FREECAD ASSEMBLY — COMPONENT RECIPES ("cad_assembly")

This assembly document has 12 components, labeled P0..P11 below (a component is one placed body or linked part). 11 of them carry a construction recipe — the FreeCAD feature program that regenerates the part from scratch, quoted from this document or its linked companion documents; the rest are supplied as boundary geometry only. No exploded tour is included for this assembly.
COMPONENT P0 — recipe-attached ("cad_top_frame", a linked part whose construction recipe lives in a companion FreeCAD document of the same project; that document's serialized recipe follows).
Construction recipe (the companion document, serialized — sketch geometry with constraints, then the solid features built on it; lengths are millimeters unless a unit is written):

FCSTD DOCUMENT  (FreeCAD 1.0R38641 +468 (Git))
Label: cad_top_frame
License: All rights reserved
LicenseURL: https://en.wikipedia.org/wiki/All_rights_reserved
objects: PartDesign::Line×8, Part::Feature×1, PartDesign::FeatureBase×1, Sketcher::SketchObject×1, PartDesign::Pocket×1, PartDesign::Body×1
note: 17 computed .brp shape members not serialized (recipe doc carries the construction recipe); baked Part::Feature solids carry a one-line shape summary decoded from their .brp

FEATURE [Part::Feature] Part__Feature  label="step"
  shape: bbox 365.1 x 369.8 x 38.23 mm, 1284 faces (baked)
FEATURE [PartDesign::FeatureBase] BaseFeature
  BaseFeature = -> Part__Feature
  Suppressed = false
FEATURE [Sketcher::SketchObject] Sketch
  ArcFitTolerance = 0
  AttachmentSupport = -> [BaseFeature]
  ExternalGeometry = -> [BaseFeature]
  FullyConstrained = true
  MakeInternals = false
  MapMode = 5
  Placement = pos=(0,0,439.5) rot=(0,0,1;0rad)
  sketch-geometry (6):
    g0: LineSegment [constr] StartX=-149.307 StartY=149.307 StartZ=0 EndX=149.307 EndY=149.307 EndZ=0
    g1: LineSegment [constr] StartX=149.307 StartY=149.307 StartZ=0 EndX=149.307 EndY=-149.307 EndZ=0
    g2: LineSegment [constr] StartX=149.307 StartY=-149.307 StartZ=0 EndX=-149.307 EndY=-149.307 EndZ=0
    g3: LineSegment [constr] StartX=-149.307 StartY=-149.307 StartZ=0 EndX=-149.307 EndY=149.307 EndZ=0
    g4: Circle CenterX=152 CenterY=0 CenterZ=0 NormalX=0 NormalY=0 NormalZ=1 AngleXU=0 Radius=1.5
    g5: Circle CenterX=-152 CenterY=0 CenterZ=0 NormalX=0 NormalY=0 NormalZ=1 AngleXU=0 Radius=1.5
  constraints (16):
    c: Coincident(g0,g1)
    c: Coincident(g1,g2)
    c: Coincident(g2,g3)
    c: Coincident(g3,g0)
    c: Horizontal(g0)
    c: Horizontal(g2)
    c: Vertical(g1)
    c: Vertical(g3)
    c: Coincident(g0,g-3)
    c: Coincident(g1,g-5)
    c: PointOnObject(g4,g-1)
    c: PointOnObject(g5,g-1)
    c: Distance(g5,g-7) = 3.5
    c: Equal(g5,g4)
    c: Radius(g4) = 1.5
    c: Distance(g4,g-8) = 3.5
FEATURE [PartDesign::Pocket] Pocket
  BaseFeature = -> BaseFeature
  Direction = (0,0,-1)
  Length = 5
  Length2 = 5
  Profile = -> Sketch
  ReferenceAxis = -> Sketch [N_Axis]
  Suppressed = false
  Type = 0
FEATURE [PartDesign::Line] HoleAxis_1  label="HoleAxis_motor_right_back"
  AttacherType = Attacher::AttachEngineLine
  AttachmentSupport = -> [Pocket]
  Length = 4.79083
  MapMode = 19
  Placement = pos=(152.8,172.15,419.5) rot=(0,-0.707107,0.707107;3.14159rad)
  ResizeMode = 1
FEATURE [PartDesign::Line] HoleAxis_2  label="HoleAxis_motor_left_back"
  AttacherType = Attacher::AttachEngineLine
  AttachmentSupport = -> [Pocket]
  Length = 4.79083
  MapMode = 19
  Placement = pos=(-152.8,172.15,419.5) rot=(1,0,0;1.5708rad)
  ResizeMode = 1
FEATURE [PartDesign::Line] HoleAxis_3  label="HoleAxis_motor_right_right"
  AttacherType = Attacher::AttachEngineLine
  AttachmentSupport = -> [Pocket]
  Length = 4.79083
  MapMode = 19
  Placement = pos=(172.15,152.8,419.5) rot=(-0.57735,-0.57735,0.57735;2.0944rad)
  ResizeMode = 1
FEATURE [PartDesign::Line] HoleAxis_4  label="HoleAxis_motor_left_left"
  AttacherType = Attacher::AttachEngineLine
  AttachmentSupport = -> [Pocket]
  Length = 4.79083
  MapMode = 19
  Placement = pos=(-172.15,152.8,419.5) rot=(0.57735,0.57735,0.57735;2.0944rad)
  ResizeMode = 1
FEATURE [PartDesign::Line] HoleAxis_5  label="HoleAxis_front_idler_right_front"
  AttacherType = Attacher::AttachEngineLine
  AttachmentSupport = -> [Pocket]
  Length = 4.79083
  MapMode = 19
  Placement = pos=(152.8,-172.15,419.5) rot=(0,0.707107,0.707107;3.14159rad)
  ResizeMode = 1
FEATURE [PartDesign::Line] HoleAxis_6  label="HoleAxis_front_idler_left_front"
  AttacherType = Attacher::AttachEngineLine
  AttachmentSupport = -> [Pocket]
  Length = 4.79083
  MapMode = 19
  Placement = pos=(-152.8,-172.15,419.5) rot=(-1,0,0;1.5708rad)
  ResizeMode = 1
FEATURE [PartDesign::Line] HoleAxis_7  label="HoleAxis_support_right"
  AttacherType = Attacher::AttachEngineLine
  AttachmentSupport = -> [Pocket]
  Length = 4.2272
  MapMode = 19
  Placement = pos=(152,0,436.9) rot=(0,0,1;0rad)
  ResizeMode = 1
FEATURE [PartDesign::Line] HoleAxis_8  label="HoleAxis_support_left"
  AttacherType = Attacher::AttachEngineLine
  AttachmentSupport = -> [Pocket]
  Length = 4.2272
  MapMode = 19
  Placement = pos=(-152,0,436.9) rot=(0,0,1;0rad)
  ResizeMode = 1
FEATURE [PartDesign::Body] Body  label="cad_top_frame"
  AllowCompound = false
  BaseFeature = -> Part__Feature
  Group = -> [BaseFeature,Sketch,Pocket,HoleAxis_1,HoleAxis_2,HoleAxis_3,HoleAxis_4,HoleAxis_5,HoleAxis_6,HoleAxis_7,HoleAxis_8]
  Origin = -> Origin
  Placement = pos=(177.5,177.5,-414.5) rot=(0,0,1;0rad)
  Tip = -> Pocket
COMPONENT P1 — geometry summary ("front_idler_left_part"; no construction recipe available for this part):
  bounding box: 54.7 x 33.8 x 26.2 mm
  tessellated surface: 4,628 triangles
  volume: 28726 mm^3 (59% of its bounding box)
COMPONENT P2 — recipe-attached ("k1_front_idler_right_part", a linked part whose construction recipe lives in a companion FreeCAD document of the same project; that document's serialized recipe follows).
Construction recipe (the companion document, serialized — sketch geometry with constraints, then the solid features built on it; lengths are millimeters unless a unit is written):

FCSTD DOCUMENT  (FreeCAD 1.0R38641 +468 (Git))
Label: k1_front_idler_right
License: All rights reserved
LicenseURL: https://en.wikipedia.org/wiki/All_rights_reserved
objects: PartDesign::Pad×11, PartDesign::Pocket×9, Sketcher::SketchObject×8, PartDesign::Line×2, App::Link×2, Part::Feature×1, PartDesign::FeatureBase×1, PartDesign::Body×1, App::Part×1
note: 82 computed .brp shape members not serialized (recipe doc carries the construction recipe); baked Part::Feature solids carry a one-line shape summary decoded from their .brp
EXTERNAL_REF file=cad_powge_pulley.FCStd obj=Part
EXTERNAL_REF file=cad_M4_DIN912_30mm.FCStd obj=Body

FEATURE [Part::Feature] Part__Feature  label="step"
  shape: bbox 25.99 x 33.8 x 47.95 mm, 40 faces (baked)
FEATURE [PartDesign::FeatureBase] BaseFeature
  BaseFeature = -> Part__Feature
  Suppressed = false
FEATURE [PartDesign::Line] HoleAxis_1  label="HoleAxis_frame"
  AttacherType = Attacher::AttachEngineLine
  AttachmentSupport = -> [BaseFeature]
  Length = 6.48171
  MapMode = 19
  Placement = pos=(-19.485,0,40.055) rot=(1,0,0;1.5708rad)
  ResizeMode = 1
FEATURE [Sketcher::SketchObject] Sketch
  ArcFitTolerance = 1e-06
  AttachmentSupport = -> [BaseFeature]
  ExternalGeometry = -> [BaseFeature]
  FullyConstrained = true
  MakeInternals = false
  MapMode = 5
  Placement = pos=(0,0,36) rot=(1,0,0;3.14159rad)
  sketch-geometry (1):
    g0: Circle CenterX=-11.5 CenterY=-17.6 CenterZ=0 NormalX=0 NormalY=0 NormalZ=1 AngleXU=0 Radius=0.75
  constraints (2):
    c: Coincident(g0,g-3)
    c: Diameter(g0) = 1.5
FEATURE [PartDesign::Pocket] Pocket
  BaseFeature = -> BaseFeature
  Direction = (0,0,1)
  Length = 5
  Length2 = 5
  Profile = -> Sketch
  ReferenceAxis = -> Sketch [N_Axis]
  Refine = true
  Suppressed = false
  Type = 1
FEATURE [PartDesign::Pocket] Pocket001
  BaseFeature = -> Pocket
  Direction = (0,0,-1)
  Length = 0.725
  Length2 = 5
  Profile = -> Pocket [Face18]
  Refine = true
  Suppressed = false
  Type = 0
FEATURE [PartDesign::Pad] Pad
  BaseFeature = -> Pocket001
  Direction = (0,0,-1)
  Length = 0.725
  Length2 = 10
  Profile = -> Pocket001 [Face34]
  Refine = true
  Suppressed = false
  Type = 0
FEATURE [PartDesign::Pad] Pad001
  BaseFeature = -> Pad
  Direction = (0,0,-1)
  Length = 0.725
  Length2 = 10
  Profile = -> Pad [Face20]
  Refine = true
  Suppressed = false
  Type = 0
FEATURE [PartDesign::Pocket] Pocket002
  BaseFeature = -> Pad001
  Direction = (0,0,-1)
  Length = 0.725
  Length2 = 5
  Profile = -> Pad001 [Face29]
  Refine = true
  Suppressed = false
  Type = 0
FEATURE [PartDesign::Pad] Pad002
  BaseFeature = -> Pocket002
  Direction = (-1,0,0)
  Length = 0.21
  Length2 = 10
  Profile = -> Pocket002 [Face4]
  Refine = true
  Suppressed = false
  Type = 0
FEATURE [PartDesign::Line] DatumLine
  AttacherType = Attacher::AttachEngineLine
  AttachmentOffset = pos=(0,0.6,0) rot=(0,0,1;0rad)
  AttachmentSupport = -> [Pad002]
  Length = 20
  MapMode = 19
  Placement = pos=(-20.105,22.365,40.945) rot=(0,0,1;0rad)
  ResizeMode = 0
FEATURE [PartDesign::Pad] Pad003
  BaseFeature = -> Pad002
  Direction = (0,0,-1)
  Length = 10
  Length2 = 10
  Profile = -> Pad002 [Face37]
  Refine = true
  Suppressed = false
  Type = 3
  UpToFace = -> Pad002 [Face35]
FEATURE [PartDesign::Pad] Pad004
  BaseFeature = -> Pad003
  Direction = (0,0,1)
  Length = 10
  Length2 = 10
  Profile = -> Pad003 [Edge84]
  Refine = true
  Suppressed = false
  Type = 3
  UpToFace = -> Pad003 [Face17]
FEATURE [PartDesign::Pad] Pad005
  BaseFeature = -> Pad004
  Direction = (0,0,1)
  Length = 10
  Length2 = 10
  Profile = -> Pad004 [Face20]
  Refine = true
  Suppressed = false
  Type = 3
  UpToFace = -> Pad004 [Face37]
FEATURE [Sketcher::SketchObject] Sketch001
  ArcFitTolerance = 1e-06
  AttachmentSupport = -> [Pad005]
  ExternalGeometry = -> [DatumLine]
  FullyConstrained = true
  MakeInternals = false
  MapMode = 5
  Placement = pos=(0,0,40.945) rot=(0,0,1;0rad)
  sketch-geometry (1):
    g0: Circle CenterX=-20.105 CenterY=22.365 CenterZ=0 NormalX=0 NormalY=0 NormalZ=1 AngleXU=0 Radius=1.6
  constraints (2):
    c: Coincident(g0,g-3)
    c: Diameter(g0) = 3.2
FEATURE [PartDesign::Pocket] Pocket003
  BaseFeature = -> Pad005
  Direction = (0,0,-1)
  Length = 0
  Length2 = 5
  Profile = -> Sketch001
  ReferenceAxis = -> Sketch001 [N_Axis]
  Refine = true
  Suppressed = false
  Type = 3
  UpToFace = -> Pad005 [Face18]
FEATURE [Sketcher::SketchObject] Sketch002
  ArcFitTolerance = 1e-06
  AttachmentSupport = -> [Pocket003]
  ExternalGeometry = -> [DatumLine]
  FullyConstrained = true
  MakeInternals = false
  MapMode = 5
  Placement = pos=(0,0,32.325) rot=(1,0,0;3.14159rad)
  sketch-geometry (1):
    g0: Circle CenterX=-20.105 CenterY=-22.365 CenterZ=0 NormalX=0 NormalY=0 NormalZ=1 AngleXU=0 Radius=2.3
  constraints (2):
    c: Coincident(g0,g-3)
    c: Diameter(g0) = 4.6
FEATURE [PartDesign::Pocket] Pocket004
  BaseFeature = -> Pocket003
  Direction = (0,0,1)
  Length = 5.1
  Length2 = 5
  Profile = -> Sketch002
  ReferenceAxis = -> Sketch002 [N_Axis]
  Refine = true
  Suppressed = false
  Type = 0
FEATURE [Sketcher::SketchObject] Sketch003
  ArcFitTolerance = 1e-06
  AttachmentSupport = -> [Pocket004]
  ExternalGeometry = -> [DatumLine,Pocket004]
  FullyConstrained = true
  MakeInternals = false
  MapMode = 5
  Placement = pos=(0,0,32.325) rot=(1,0,0;3.14159rad)
  sketch-geometry (4):
    g0: ArcOfCircle CenterX=-20.105 CenterY=-22.365 CenterZ=0 NormalX=0 NormalY=0 NormalZ=1 AngleXU=0 Radius=4 StartAngle=0 EndAngle=3.14159
    g1: LineSegment StartX=-16.105 StartY=-22.365 StartZ=0 EndX=-16.105 EndY=-24 EndZ=0
    g2: LineSegment StartX=-16.105 StartY=-24 StartZ=0 EndX=-24.105 EndY=-24 EndZ=0
    g3: LineSegment StartX=-24.105 StartY=-24 StartZ=0 EndX=-24.105 EndY=-22.365 EndZ=0
  constraints (10):
    c: Coincident(g0,g-3)
    c: PointOnObject(g1,g-4)
    c: Vertical(g1)
    c: Coincident(g2,g1)
    c: Horizontal(g2)
    c: Coincident(g3,g2)
    c: Vertical(g3)
    c: Radius(g0) = 4
    c: Tangent(g1,g0) = 1.5708
    c: Tangent(g3,g0) = 1.5708
FEATURE [PartDesign::Pocket] Pocket005
  BaseFeature = -> Pocket004
  Direction = (0,0,1)
  Length = 8
  Length2 = 5
  Profile = -> Sketch003
  ReferenceAxis = -> Sketch003 [N_Axis]
  Refine = true
  Reversed = true
  Suppressed = false
  Type = 0
FEATURE [PartDesign::Pad] Pad006
  BaseFeature = -> Pocket005
  Direction = (0,0,-1)
  Length = 6.72
  Length2 = 10
  Profile = -> Pocket005 [Face12]
  Refine = true
  Suppressed = false
  Type = 0
FEATURE [Sketcher::SketchObject] Sketch004
  ArcFitTolerance = 1e-06
  AttachmentSupport = -> [Pad006]
  ExternalGeometry = -> [Pad006]
  FullyConstrained = true
  MakeInternals = false
  MapMode = 5
  Placement = pos=(0,0,0.2) rot=(1,0,0;3.14159rad)
  sketch-geometry (2):
    g0: Circle CenterX=-11.5 CenterY=-17.6 CenterZ=0 NormalX=0 NormalY=0 NormalZ=1 AngleXU=0 Radius=4.5
    g1: Circle CenterX=-11.5 CenterY=-17.6 CenterZ=0 NormalX=0 NormalY=0 NormalZ=1 AngleXU=0 Radius=1.9
  constraints (4):
    c: Coincident(g0,g-3)
    c: Equal(g0,g-3)
    c: Coincident(g1,g0)
    c: Diameter(g1) = 3.8
FEATURE [PartDesign::Pad] Pad007
  BaseFeature = -> Pad006
  Direction = (0,0,-1)
  Length = 5
  Length2 = 10
  Profile = -> Sketch004
  ReferenceAxis = -> Sketch004 [N_Axis]
  Refine = true
  Reversed = true
  Suppressed = false
  Type = 0
FEATURE [Sketcher::SketchObject] Sketch005
  ArcFitTolerance = 1e-06
  AttachmentSupport = -> [Pad007]
  ExternalGeometry = -> [Pad007]
  FullyConstrained = true
  MakeInternals = false
  MapMode = 5
  Placement = pos=(0,0,0.2) rot=(1,0,0;3.14159rad)
  sketch-geometry (2):
    g0: Circle CenterX=-11.5 CenterY=-17.6 CenterZ=0 NormalX=0 NormalY=0 NormalZ=1 AngleXU=0 Radius=4.5
    g1: Circle CenterX=-11.5 CenterY=-17.6 CenterZ=0 NormalX=0 NormalY=0 NormalZ=1 AngleXU=0 Radius=3.6
  constraints (4):
    c: Coincident(g0,g-3)
    c: Equal(g0,g-3)
    c: Coincident(g1,g0)
    c: Diameter(g1) = 7.2
FEATURE [PartDesign::Pad] Pad008
  BaseFeature = -> Pad007
  Direction = (0,0,-1)
  Length = 10
  Length2 = 10
  Profile = -> Sketch005
  ReferenceAxis = -> Sketch005 [N_Axis]
  Refine = true
  Suppressed = false
  Type = 3
  UpToFace = -> Pad007 [Face1]
FEATURE [PartDesign::Pocket] Pocket006
  BaseFeature = -> Pad008
  Direction = (0,0,-1)
  Length = 0.3
  Length2 = 5
  Profile = -> Pad008 [Face14]
  Refine = true
  Suppressed = false
  Type = 0
FEATURE [PartDesign::Pad] Pad009
  BaseFeature = -> Pocket006
  Direction = (0,0,-1)
  Length = 0.3
  Length2 = 10
  Profile = -> Pocket006 [Face11]
  Refine = true
  Suppressed = false
  Type = 0
FEATURE [PartDesign::Pad] Pad010
  BaseFeature = -> Pad009
  Direction = (0,0,-1)
  Length = 0.3
  Length2 = 10
  Profile = -> Pad009 [Face32]
  Refine = true
  Suppressed = false
  Type = 0
FEATURE [App::Link] Link  label="cad_powge_pulley_link"
  LinkPlacement = pos=(-11.5,17.6,9.7) rot=(0,0,1;0rad)
  LinkedObject = -> <external cad_powge_pulley.FCStd>#Part
  Placement = pos=(-11.5,17.6,9.7) rot=(0,0,1;0rad)
FEATURE [Sketcher::SketchObject] Sketch006
  ArcFitTolerance = 1e-06
  AttachmentSupport = -> [Pad010]
  ExternalGeometry = -> [Pad010]
  FullyConstrained = true
  MakeInternals = false
  MapMode = 5
  Placement = pos=(0,0,47.945) rot=(0,0,1;0rad)
  sketch-geometry (3):
    g0: LineSegment StartX=-26.2 StartY=0 StartZ=0 EndX=-25.2 EndY=0 EndZ=0
    g1: LineSegment StartX=-26.2 StartY=0 StartZ=0 EndX=-26.2 EndY=14.265 EndZ=0
    g2: LineSegment StartX=-26.2 StartY=14.265 StartZ=0 EndX=-25.2 EndY=0 EndZ=0
  constraints (7):
    c: Coincident(g0,g-3)
    c: PointOnObject(g0,g-1)
    c: Coincident(g1,g0)
    c: Coincident(g1,g-3)
    c: Coincident(g2,g1)
    c: Coincident(g2,g0)
    c: Distance(g0,g0) = 1
FEATURE [PartDesign::Pocket] Pocket007
  BaseFeature = -> Pad010
  Direction = (0,0,-1)
  Length = 5
  Length2 = 5
  Profile = -> Sketch006
  ReferenceAxis = -> Sketch006 [N_Axis]
  Refine = true
  Suppressed = false
  Type = 1
FEATURE [App::Link] Link001  label="cad_m4_din912_30_link"
  LinkPlacement = pos=(-11.5,17.6,-3.8) rot=(0,0,1;0rad)
  LinkedObject = -> <external cad_M4_DIN912_30mm.FCStd>#Body
  Placement = pos=(-11.5,17.6,-3.8) rot=(0,0,1;0rad)
FEATURE [Sketcher::SketchObject] Sketch007
  ArcFitTolerance = 1e-06
  AttachmentSupport = -> [Pocket007]
  ExternalGeometry = -> [Pocket007]
  FullyConstrained = true
  MakeInternals = false
  MapMode = 5
  Placement = pos=(0,0,0) rot=(0.57735,0.57735,0.57735;2.0944rad)
  sketch-geometry (2):
    g0: LineSegment [constr] StartX=19.265 StartY=40.055 StartZ=0 EndX=19.265 EndY=4.985 EndZ=0
    g1: Circle CenterX=19.265 CenterY=24.78 CenterZ=0 NormalX=0 NormalY=0 NormalZ=1 AngleXU=0 Radius=2.3
  constraints (5):
    c: Coincident(g0,g-3)
    c: Coincident(g0,g-4)
    c: PointOnObject(g1,g0)
    c: Equal(g1,g-3)
    c: Distance(g1,g-5) = 31.5
FEATURE [PartDesign::Pocket] Pocket008
  BaseFeature = -> Pocket007
  Direction = (-1,0,0)
  Length = 1
  Length2 = 5
  Profile = -> Sketch007
  ReferenceAxis = -> Sketch007 [N_Axis]
  Refine = true
  Suppressed = false
  Type = 0
FEATURE [PartDesign::Body] Body  label="k1_front_idler_right"
  AllowCompound = false
  BaseFeature = -> Part__Feature
  Group = -> [BaseFeature,HoleAxis_1,Sketch,Pocket,Pocket001,Pad,Pad001,Pocket002,Pad002,DatumLine,Pad003,Pad004,Pad005,Sketch001,Pocket003,Sketch002,Pocket004,Sketch003,Pocket005,Pad006,Sketch004,Pad007,Sketch005,Pad008,Pocket006,Pad009,Pad010,Sketch006,Pocket007,Sketch007,Pocket008]
  Origin = -> Origin
  Tip = -> Pocket008
FEATURE [App::Part] Part  label="k1_front_idler_right_part"
  Group = -> [Part__Feature,Body,Link,Link001]
  Origin = -> Origin001
  Placement = pos=(0,0,0) rot=(0,0,1;3.14159rad)
COMPONENT P3 — recipe-attached ("k1_motor_mount_stock_left_part", a linked part whose construction recipe lives in a companion FreeCAD document of the same project; that document's serialized recipe follows).
Construction recipe (the companion document, serialized — sketch geometry with constraints, then the solid features built on it; lengths are millimeters unless a unit is written):

FCSTD DOCUMENT  (FreeCAD 1.0R38641 +468 (Git))
Label: k1_motor_mount_stock_left
License: All rights reserved
LicenseURL: https://en.wikipedia.org/wiki/All_rights_reserved
objects: App::Link×9, PartDesign::Pocket×6, Sketcher::SketchObject×5, PartDesign::Pad×2, Part::Feature×1, PartDesign::FeatureBase×1, PartDesign::Body×1, App::Part×1
note: 38 computed .brp shape members not serialized (recipe doc carries the construction recipe); baked Part::Feature solids carry a one-line shape summary decoded from their .brp
EXTERNAL_REF file=cad_powge_pulley.FCStd obj=Part
EXTERNAL_REF file=cad_mf95zz.FCStd obj=Body
EXTERNAL_REF file=cad_motor_shaft_55mm.FCStd obj=Part__Feature
EXTERNAL_REF file=cad_20T_15mm_pulley.FCStd obj=Part
EXTERNAL_REF file=cad_nema17_42_60.FCStd obj=COMPOUND049
EXTERNAL_REF file=cad_diaphragm_coupler.FCStd obj=_764K239_NO_THREADS_Servomotor_Precision_Flexible_Shaft_Coupling013
EXTERNAL_REF file=cad_m4_35mm.FCStd obj=Part__Feature

FEATURE [Part::Feature] Part__Feature  label="step"
  shape: bbox 73.5 x 47.7 x 110.9 mm, 153 faces (baked)
FEATURE [PartDesign::FeatureBase] BaseFeature
  BaseFeature = -> Part__Feature
  Suppressed = false
FEATURE [App::Link] Link  label="cad_powge_pulley_top_link"
  LinkPlacement = pos=(14.1406,100.078,20.85) rot=(0,0,1;0rad)
  LinkedObject = -> <external cad_powge_pulley.FCStd>#Part
  Placement = pos=(14.1406,100.078,20.85) rot=(0,0,1;0rad)
FEATURE [App::Link] Link001  label="cad_powge_pulley_bottom_link"
  LinkPlacement = pos=(14.1406,100.078,9.7) rot=(0,0,1;0rad)
  LinkedObject = -> <external cad_powge_pulley.FCStd>#Part
  Placement = pos=(14.1406,100.078,9.7) rot=(0,0,1;0rad)
FEATURE [App::Link] Link002  label="cad_mf95zz_top_link"
  LinkPlacement = pos=(29.6406,84.5783,37.2) rot=(0,1,0;3.14159rad)
  LinkedObject = -> <external cad_mf95zz.FCStd>#Body
  Placement = pos=(29.6406,84.5783,37.2) rot=(0,1,0;3.14159rad)
FEATURE [App::Link] Link003  label="cad_mf95zz_bottom_link"
  LinkPlacement = pos=(29.6406,84.5783,-4.4) rot=(0,0,1;3.14159rad)
  LinkedObject = -> <external cad_mf95zz.FCStd>#Body
  Placement = pos=(29.6406,84.5783,-4.4) rot=(0,0,1;3.14159rad)
FEATURE [App::Link] Link004  label="cad_motor_shaft_55mm_link"
  LinkPlacement = pos=(370.445,-290.422,175.11) rot=(0,0,1;0rad)
  LinkedObject = -> <external cad_motor_shaft_55mm.FCStd>#Part__Feature
  Placement = pos=(370.445,-290.422,175.11) rot=(0,0,1;0rad)
FEATURE [App::Link] Link005  label="cad_20T_15mm_pulley_link"
  LinkPlacement = pos=(117.263,15.5011,1.55198) rot=(0,1,0;3.14159rad)
  LinkedObject = -> <external cad_20T_15mm_pulley.FCStd>#Part
  Placement = pos=(117.263,15.5011,1.55198) rot=(0,1,0;3.14159rad)
FEATURE [App::Link] Link006  label="cad_nema17_42_60_link"
  LinkPlacement = pos=(29.6406,84.5783,-79.702) rot=(0,0,1;0rad)
  LinkedObject = -> <external cad_nema17_42_60.FCStd>#COMPOUND049
  Placement = pos=(29.6406,84.5783,-79.702) rot=(0,0,1;0rad)
FEATURE [App::Link] Link007  label="cad_diaphragm_coupler_5_5_link"
  LinkPlacement = pos=(370.37,-290.416,168.405) rot=(0,0,1;0rad)
  LinkedObject = -> <external cad_diaphragm_coupler.FCStd>#_764K239_NO_THREADS_Servomotor_Precision_Flexible_Shaft_Coupling013
  Placement = pos=(370.37,-290.416,168.405) rot=(0,0,1;0rad)
FEATURE [App::Link] Link008  label="cad_m4_35mm_link"
  LinkPlacement = pos=(14.1406,100.078,0.376278) rot=(0,0,1;0rad)
  LinkedObject = -> <external cad_m4_35mm.FCStd>#Part__Feature
  Placement = pos=(14.1406,100.078,0.376278) rot=(0,0,1;0rad)
FEATURE [Sketcher::SketchObject] Sketch
  ArcFitTolerance = 1e-06
  AttachmentSupport = -> [BaseFeature]
  ExternalGeometry = -> [BaseFeature]
  FullyConstrained = true
  MakeInternals = false
  MapMode = 5
  Placement = pos=(8.1168e-12,-2.90335e-11,-57) rot=(0,0,1;0rad)
  sketch-geometry (6):
    g0: LineSegment StartX=52.6406 StartY=970.078 StartZ=0 EndX=59.1406 EndY=963.578 EndZ=0
    g1: LineSegment StartX=100.141 StartY=963.578 StartZ=0 EndX=106.641 EndY=970.078 EndZ=0
    g2: LineSegment StartX=106.641 StartY=970.078 StartZ=0 EndX=106.641 EndY=963.578 EndZ=0
    g3: LineSegment StartX=100.141 StartY=963.578 StartZ=0 EndX=106.641 EndY=963.578 EndZ=0
    g4: LineSegment StartX=52.6406 StartY=970.078 StartZ=0 EndX=52.6406 EndY=963.578 EndZ=0
    g5: LineSegment StartX=59.1406 StartY=963.578 StartZ=0 EndX=52.6406 EndY=963.578 EndZ=0
  constraints (14):
    c: Coincident(g0,g-3)
    c: Coincident(g0,g-4)
    c: Coincident(g1,g-4)
    c: Coincident(g1,g-5)
    c: Coincident(g2,g1)
    c: Vertical(g2)
    c: Coincident(g3,g1)
    c: Coincident(g3,g2)
    c: Horizontal(g3)
    c: Coincident(g4,g0)
    c: Vertical(g4)
    c: Coincident(g5,g0)
    c: Coincident(g5,g4)
    c: Horizontal(g5)
FEATURE [PartDesign::Pocket] Pocket
  BaseFeature = -> BaseFeature
  Direction = (1.424e-13,-5.094e-13,-1)
  Length = 6
  Length2 = 5
  Profile = -> Sketch
  ReferenceAxis = -> Sketch [N_Axis]
  Refine = true
  Suppressed = false
  Type = 0
FEATURE [Sketcher::SketchObject] Sketch001
  ArcFitTolerance = 1e-06
  AttachmentSupport = -> [Pocket]
  ExternalGeometry = -> [Pocket]
  FullyConstrained = true
  MakeInternals = false
  MapMode = 5
  Placement = pos=(4.7e-13,-2.35e-13,-63) rot=(1,0,0;3.14159rad)
  sketch-geometry (2):
    g0: Circle CenterX=79.6406 CenterY=-984.578 CenterZ=0 NormalX=0 NormalY=0 NormalZ=1 AngleXU=0 Radius=15
    g1: Circle CenterX=79.6406 CenterY=-984.578 CenterZ=0 NormalX=0 NormalY=0 NormalZ=1 AngleXU=0 Radius=14
  constraints (4):
    c: Coincident(g0,g-3)
    c: Equal(g0,g-3)
    c: Coincident(g1,g0)
    c: Diameter(g1) = 28
FEATURE [PartDesign::Pad] Pad
  BaseFeature = -> Pocket
  Direction = (7.5e-15,-3.7e-15,-1)
  Length = 10
  Length2 = 10
  Profile = -> Sketch001
  ReferenceAxis = -> Sketch001 [N_Axis]
  Refine = true
  Suppressed = false
  Type = 3
  UpToFace = -> Pocket [Face9]
FEATURE [PartDesign::Pocket] Pocket001
  BaseFeature = -> Pad
  Direction = (7e-15,-2.3e-15,-1)
  Length = 0
  Length2 = 5
  Profile = -> Pad [Face8]
  Refine = true
  Suppressed = false
  Type = 3
  UpToFace = -> Pad [Face7]
FEATURE [Sketcher::SketchObject] Sketch002
  ArcFitTolerance = 1e-06
  AttachmentSupport = -> [Pocket001]
  ExternalGeometry = -> [Pocket001]
  FullyConstrained = true
  MakeInternals = false
  MapMode = 5
  Placement = pos=(1.5407e-12,-1.06128e-11,-57) rot=(0,0,1;0rad)
  sketch-geometry (4):
    g0: LineSegment StartX=79.6406 StartY=984.578 StartZ=0 EndX=65.6406 EndY=984.578 EndZ=0
    g1: LineSegment StartX=65.6406 StartY=984.578 StartZ=0 EndX=65.6406 EndY=976.278 EndZ=0
    g2: LineSegment StartX=65.6406 StartY=976.278 StartZ=0 EndX=79.6406 EndY=976.278 EndZ=0
    g3: LineSegment StartX=79.6406 StartY=976.278 StartZ=0 EndX=79.6406 EndY=984.578 EndZ=0
  constraints (11):
    c: Coincident(g0,g1)
    c: Coincident(g1,g2)
    c: Coincident(g2,g3)
    c: Coincident(g3,g0)
    c: Horizontal(g0)
    c: Horizontal(g2)
    c: Vertical(g1)
    c: Vertical(g3)
    c: Coincident(g0,g-4)
    c: PointOnObject(g1,g-3)
    c: Tangent(g1,g-4)
FEATURE [PartDesign::Pocket] Pocket002
  BaseFeature = -> Pocket001
  Direction = (2.7e-14,-1.862e-13,-1)
  Length = 0
  Length2 = 5
  Profile = -> Sketch002
  ReferenceAxis = -> Sketch002 [N_Axis]
  Refine = true
  Suppressed = false
  Type = 3
  UpToFace = -> Pocket001 [Face8]
FEATURE [Sketcher::SketchObject] Sketch003
  ArcFitTolerance = 1e-06
  AttachmentSupport = -> [Pocket002]
  ExternalGeometry = -> [Pocket002]
  FullyConstrained = true
  MakeInternals = false
  MapMode = 5
  Placement = pos=(2.15318e-10,976.278,-3.51773e-10) rot=(1,0,0;1.5708rad)
  sketch-geometry (4):
    g0: LineSegment StartX=81.1406 StartY=-10 StartZ=0 EndX=65.2906 EndY=-10 EndZ=0
    g1: LineSegment StartX=65.2906 StartY=-10 StartZ=0 EndX=65.2906 EndY=-57 EndZ=0
    g2: LineSegment StartX=65.2906 StartY=-57 StartZ=0 EndX=81.1406 EndY=-57 EndZ=0
    g3: LineSegment StartX=81.1406 StartY=-57 StartZ=0 EndX=81.1406 EndY=-10 EndZ=0
  constraints (11):
    c: Coincident(g0,g1)
    c: Coincident(g1,g2)
    c: Coincident(g2,g3)
    c: Coincident(g3,g0)
    c: Horizontal(g0)
    c: Horizontal(g2)
    c: Vertical(g1)
    c: Vertical(g3)
    c: Coincident(g0,g-4)
    c: PointOnObject(g1,g-5)
    c: PointOnObject(g0,g-3)
FEATURE [PartDesign::Pocket] Pocket003
  BaseFeature = -> Pocket002
  Direction = (2.205e-13,1,-3.604e-13)
  Length = 0
  Length2 = 5
  Profile = -> Sketch003
  ReferenceAxis = -> Sketch003 [N_Axis]
  Refine = true
  Suppressed = false
  Type = 3
  UpToFace = -> Pocket002 [Face84]
FEATURE [Sketcher::SketchObject] Sketch004
  ArcFitTolerance = 1e-06
  AttachmentSupport = -> [Pocket003]
  ExternalGeometry = -> [Pocket003]
  FullyConstrained = true
  MakeInternals = false
  MapMode = 5
  Placement = pos=(-3.6022e-10,985.528,-2.02575e-10) rot=(1,0,0;1.5708rad)
  sketch-geometry (4):
    g0: LineSegment StartX=86.1406 StartY=-10 StartZ=0 EndX=86.1406 EndY=-57 EndZ=0
    g1: LineSegment StartX=86.1406 StartY=-57 StartZ=0 EndX=93.9906 EndY=-57 EndZ=0
    g2: LineSegment StartX=93.9906 StartY=-57 StartZ=0 EndX=93.9906 EndY=-10 EndZ=0
    g3: LineSegment StartX=93.9906 StartY=-10 StartZ=0 EndX=86.1406 EndY=-10 EndZ=0
  constraints (11):
    c: Coincident(g0,g1)
    c: Coincident(g1,g2)
    c: Coincident(g2,g3)
    c: Coincident(g3,g0)
    c: Vertical(g0)
    c: Vertical(g2)
    c: Horizontal(g1)
    c: Horizontal(g3)
    c: Coincident(g0,g-4)
    c: PointOnObject(g1,g-5)
    c: PointOnObject(g2,g-3)
FEATURE [PartDesign::Pocket] Pocket004
  BaseFeature = -> Pocket003
  Direction = (-3.655e-13,1,-2.056e-13)
  Length = 0
  Length2 = 5
  Profile = -> Sketch004
  ReferenceAxis = -> Sketch004 [N_Axis]
  Refine = true
  Suppressed = false
  Type = 3
  UpToFace = -> Pocket003 [Face53]
FEATURE [PartDesign::Pad] Pad001
  BaseFeature = -> Pocket004
  Direction = (-1,0,-7.7e-15)
  Length = 10
  Length2 = 10
  Profile = -> Pocket004 [Face14]
  Refine = true
  Suppressed = false
  Type = 3
  UpToFace = -> Pocket004 [Face44]
FEATURE [PartDesign::Pocket] Pocket005
  BaseFeature = -> Pad001
  Direction = (2e-16,4.8e-15,1)
  Length = 5
  Length2 = 5
  Profile = -> Pad001 [Face154]
  Refine = true
  Suppressed = false
  Type = 1
FEATURE [PartDesign::Body] Body  label="k1_motor_mount_stock_left"
  AllowCompound = false
  BaseFeature = -> Part__Feature
  Group = -> [BaseFeature,Sketch,Pocket,Sketch001,Pad,Pocket001,Sketch002,Pocket002,Sketch003,Pocket003,Sketch004,Pocket004,Pad001,Pocket005]
  Origin = -> Origin
  Placement = pos=(-50,-900,0) rot=(0,0,1;0rad)
  Tip = -> Pocket005
FEATURE [App::Part] Part  label="k1_motor_mount_stock_left_part"
  Group = -> [Part__Feature,Body,Link,Link001,Link002,Link003,Link004,Link005,Link006,Link007,Link008]
  Origin = -> Origin001
COMPONENT P4 — recipe-attached ("k1_motor_mount_stock_right_part", a linked part whose construction recipe lives in a companion FreeCAD document of the same project; that document's serialized recipe follows).
Construction recipe (the companion document, serialized — sketch geometry with constraints, then the solid features built on it; lengths are millimeters unless a unit is written):

FCSTD DOCUMENT  (FreeCAD 1.0R38641 +468 (Git))
Label: k1_motor_mount_stock_right
License: All rights reserved
LicenseURL: https://en.wikipedia.org/wiki/All_rights_reserved
objects: App::Link×9, PartDesign::Pocket×6, Sketcher::SketchObject×5, PartDesign::Pad×2, Part::Feature×1, PartDesign::FeatureBase×1, PartDesign::Body×1, App::Part×1
note: 38 computed .brp shape members not serialized (recipe doc carries the construction recipe); baked Part::Feature solids carry a one-line shape summary decoded from their .brp
EXTERNAL_REF file=cad_powge_pulley.FCStd obj=Part
EXTERNAL_REF file=cad_20T_15mm_pulley.FCStd obj=Part
EXTERNAL_REF file=cad_mf95zz.FCStd obj=Body
EXTERNAL_REF file=cad_diaphragm_coupler.FCStd obj=_764K239_NO_THREADS_Servomotor_Precision_Flexible_Shaft_Coupling013
EXTERNAL_REF file=cad_nema17_42_60.FCStd obj=COMPOUND049
EXTERNAL_REF file=cad_motor_shaft_55mm.FCStd obj=Part__Feature
EXTERNAL_REF file=cad_m4_35mm.FCStd obj=Part__Feature

FEATURE [Part::Feature] Part__Feature  label="step"
  shape: bbox 73.5 x 47.7 x 110.9 mm, 157 faces (baked)
FEATURE [PartDesign::FeatureBase] BaseFeature
  BaseFeature = -> Part__Feature
  Suppressed = false
FEATURE [App::Link] Link  label="cad_powge_pulley_top_link"
  LinkPlacement = pos=(94.1406,100.078,88.8) rot=(0,0,1;0rad)
  LinkedObject = -> <external cad_powge_pulley.FCStd>#Part
  Placement = pos=(94.1406,100.078,88.8) rot=(0,0,1;0rad)
FEATURE [App::Link] Link001  label="cad_powge_pulley_bottom_link"
  LinkPlacement = pos=(94.1406,100.078,77.7) rot=(0,0,1;0rad)
  LinkedObject = -> <external cad_powge_pulley.FCStd>#Part
  Placement = pos=(94.1406,100.078,77.7) rot=(0,0,1;0rad)
FEATURE [App::Link] Link002  label="cad_20T_15mm_pulley_link"
  LinkPlacement = pos=(-8.98206,15.5009,105.208) rot=(0,-1.00667,0;0rad)
  LinkedObject = -> <external cad_20T_15mm_pulley.FCStd>#Part
  Placement = pos=(-8.98206,15.5009,105.208) rot=(0,-1.00667,0;0rad)
FEATURE [App::Link] Link003  label="cad_mf95zz_top_link"
  LinkPlacement = pos=(78.6406,84.5783,105.2) rot=(0,1,0;3.14159rad)
  LinkedObject = -> <external cad_mf95zz.FCStd>#Body
  Placement = pos=(78.6406,84.5783,105.2) rot=(0,1,0;3.14159rad)
FEATURE [App::Link] Link004  label="cad_mf95zz_bottom_link"
  LinkPlacement = pos=(78.6406,84.5783,63.6) rot=(0,0,1;0rad)
  LinkedObject = -> <external cad_mf95zz.FCStd>#Body
  Placement = pos=(78.6406,84.5783,63.6) rot=(0,0,1;0rad)
FEATURE [App::Link] Link005  label="cad_diaphragm_coupler_5_5_link001"
  LinkPlacement = pos=(419.37,-290.416,235.548) rot=(0,0,1;0rad)
  LinkedObject = -> <external cad_diaphragm_coupler.FCStd>#_764K239_NO_THREADS_Servomotor_Precision_Flexible_Shaft_Coupling013
  Placement = pos=(419.37,-290.416,235.548) rot=(0,0,1;0rad)
FEATURE [App::Link] Link006  label="cad_nema17_42_60_link"
  LinkPlacement = pos=(78.6406,84.5783,-11.702) rot=(0,0,1;3.14159rad)
  LinkedObject = -> <external cad_nema17_42_60.FCStd>#COMPOUND049
  Placement = pos=(78.6406,84.5783,-11.702) rot=(0,0,1;3.14159rad)
FEATURE [App::Link] Link007  label="cad_motor_shaft_55mm_link"
  LinkPlacement = pos=(419.445,-290.422,242.202) rot=(0,0,1;0rad)
  LinkedObject = -> <external cad_motor_shaft_55mm.FCStd>#Part__Feature
  Placement = pos=(419.445,-290.422,242.202) rot=(0,0,1;0rad)
FEATURE [App::Link] Link008  label="cad_m4_35mm_link"
  LinkPlacement = pos=(94.1406,100.078,68.3263) rot=(0,0,1;0rad)
  LinkedObject = -> <external cad_m4_35mm.FCStd>#Part__Feature
  Placement = pos=(94.1406,100.078,68.3263) rot=(0,0,1;0rad)
FEATURE [Sketcher::SketchObject] Sketch
  ArcFitTolerance = 1e-06
  AttachmentSupport = -> [BaseFeature]
  ExternalGeometry = -> [BaseFeature]
  FullyConstrained = true
  MakeInternals = false
  MapMode = 5
  Placement = pos=(1.30969e-11,5.63274e-11,-57) rot=(0,0,1;0rad)
  sketch-geometry (6):
    g0: LineSegment StartX=251.641 StartY=970.078 StartZ=0 EndX=258.141 EndY=963.578 EndZ=0
    g1: LineSegment StartX=299.141 StartY=963.578 StartZ=0 EndX=305.641 EndY=970.078 EndZ=0
    g2: LineSegment StartX=251.641 StartY=970.078 StartZ=0 EndX=251.641 EndY=963.578 EndZ=0
    g3: LineSegment StartX=258.141 StartY=963.578 StartZ=0 EndX=251.641 EndY=963.578 EndZ=0
    g4: LineSegment StartX=299.141 StartY=963.578 StartZ=0 EndX=305.641 EndY=963.578 EndZ=0
    g5: LineSegment StartX=305.641 StartY=963.578 StartZ=0 EndX=305.641 EndY=970.078 EndZ=0
  constraints (14):
    c: Coincident(g0,g-3)
    c: Coincident(g0,g-4)
    c: Coincident(g1,g-4)
    c: Coincident(g1,g-5)
    c: Coincident(g2,g0)
    c: Vertical(g2)
    c: Coincident(g3,g0)
    c: Coincident(g3,g2)
    c: Horizontal(g3)
    c: Coincident(g4,g1)
    c: Horizontal(g4)
    c: Coincident(g5,g4)
    c: Coincident(g5,g1)
    c: Vertical(g5)
FEATURE [PartDesign::Pocket] Pocket
  BaseFeature = -> BaseFeature
  Direction = (2.298e-13,9.882e-13,-1)
  Length = 6
  Length2 = 5
  Profile = -> Sketch
  ReferenceAxis = -> Sketch [N_Axis]
  Refine = true
  Suppressed = false
  Type = 0
FEATURE [Sketcher::SketchObject] Sketch001
  ArcFitTolerance = 1e-06
  AttachmentSupport = -> [Pocket]
  ExternalGeometry = -> [Pocket]
  FullyConstrained = true
  MakeInternals = false
  MapMode = 5
  Placement = pos=(-1.672e-12,-6.7271e-12,-63) rot=(1,0,0;3.14159rad)
  sketch-geometry (2):
    g0: Circle CenterX=278.641 CenterY=-984.578 CenterZ=0 NormalX=0 NormalY=0 NormalZ=1 AngleXU=0 Radius=15
    g1: Circle CenterX=278.641 CenterY=-984.578 CenterZ=0 NormalX=0 NormalY=0 NormalZ=1 AngleXU=0 Radius=14
  constraints (4):
    c: Coincident(g0,g-3)
    c: Equal(g0,g-3)
    c: Coincident(g1,g0)
    c: Diameter(g1) = 28
FEATURE [PartDesign::Pad] Pad
  BaseFeature = -> Pocket
  Direction = (-2.65e-14,-1.068e-13,-1)
  Length = 10
  Length2 = 10
  Profile = -> Sketch001
  ReferenceAxis = -> Sketch001 [N_Axis]
  Refine = true
  Suppressed = false
  Type = 3
  UpToFace = -> Pocket [Face26]
FEATURE [PartDesign::Pocket] Pocket001
  BaseFeature = -> Pad
  Direction = (-2.24e-14,-1.028e-13,-1)
  Length = 0
  Length2 = 5
  Profile = -> Pad [Face27]
  Refine = true
  Suppressed = false
  Type = 3
  UpToFace = -> Pad [Face24]
FEATURE [Sketcher::SketchObject] Sketch002
  ArcFitTolerance = 1e-06
  AttachmentSupport = -> [Pocket001]
  ExternalGeometry = -> [Pocket001]
  FullyConstrained = true
  MakeInternals = false
  MapMode = 5
  Placement = pos=(8.3152e-12,4.16619e-11,-57) rot=(0,0,1;0rad)
  sketch-geometry (4):
    g0: LineSegment StartX=278.641 StartY=984.578 StartZ=0 EndX=278.641 EndY=976.278 EndZ=0
    g1: LineSegment StartX=278.641 StartY=976.278 StartZ=0 EndX=292.641 EndY=976.278 EndZ=0
    g2: LineSegment StartX=292.641 StartY=976.278 StartZ=0 EndX=292.641 EndY=984.578 EndZ=0
    g3: LineSegment StartX=292.641 StartY=984.578 StartZ=0 EndX=278.641 EndY=984.578 EndZ=0
  constraints (11):
    c: Coincident(g0,g1)
    c: Coincident(g1,g2)
    c: Coincident(g2,g3)
    c: Coincident(g3,g0)
    c: Vertical(g0)
    c: Vertical(g2)
    c: Horizontal(g1)
    c: Horizontal(g3)
    c: Coincident(g0,g-4)
    c: PointOnObject(g1,g-3)
    c: Tangent(g2,g-4)
FEATURE [PartDesign::Pocket] Pocket002
  BaseFeature = -> Pocket001
  Direction = (1.459e-13,7.309e-13,-1)
  Length = 0
  Length2 = 5
  Profile = -> Sketch002
  ReferenceAxis = -> Sketch002 [N_Axis]
  Refine = true
  Suppressed = false
  Type = 3
  UpToFace = -> Pocket001 [Face30]
FEATURE [Sketcher::SketchObject] Sketch003
  ArcFitTolerance = 1e-06
  AttachmentSupport = -> [Pocket002]
  ExternalGeometry = -> [Pocket002]
  FullyConstrained = true
  MakeInternals = false
  MapMode = 5
  Placement = pos=(1.16e-09,976.278,-5.7864e-11) rot=(1,0,0;1.5708rad)
  sketch-geometry (4):
    g0: LineSegment StartX=277.141 StartY=-10 StartZ=0 EndX=277.141 EndY=-57 EndZ=0
    g1: LineSegment StartX=277.141 StartY=-57 StartZ=0 EndX=292.991 EndY=-57 EndZ=0
    g2: LineSegment StartX=292.991 StartY=-57 StartZ=0 EndX=292.991 EndY=-10 EndZ=0
    g3: LineSegment StartX=292.991 StartY=-10 StartZ=0 EndX=277.141 EndY=-10 EndZ=0
  constraints (11):
    c: Coincident(g0,g1)
    c: Coincident(g1,g2)
    c: Coincident(g2,g3)
    c: Coincident(g3,g0)
    c: Vertical(g0)
    c: Vertical(g2)
    c: Horizontal(g1)
    c: Horizontal(g3)
    c: Coincident(g0,g-5)
    c: PointOnObject(g1,g-6)
    c: PointOnObject(g2,g-3)
FEATURE [PartDesign::Pocket] Pocket003
  BaseFeature = -> Pocket002
  Direction = (1.1882e-12,1,-5.91e-14)
  Length = 0
  Length2 = 5
  Profile = -> Sketch003
  ReferenceAxis = -> Sketch003 [N_Axis]
  Refine = true
  Suppressed = false
  Type = 3
  UpToFace = -> Pocket002 [Face76]
FEATURE [Sketcher::SketchObject] Sketch004
  ArcFitTolerance = 1e-06
  AttachmentSupport = -> [Pocket003]
  ExternalGeometry = -> [Pocket003]
  FullyConstrained = true
  MakeInternals = false
  MapMode = 5
  Placement = pos=(-3.63e-10,985.528,4.51421e-10) rot=(1,0,0;1.5708rad)
  sketch-geometry (8):
    g0: LineSegment StartX=264.291 StartY=-57 StartZ=0 EndX=272.141 EndY=-57 EndZ=0
    g1: LineSegment StartX=272.141 StartY=-57 StartZ=0 EndX=272.141 EndY=-10 EndZ=0
    g2: LineSegment StartX=272.141 StartY=-10 StartZ=0 EndX=264.291 EndY=-10 EndZ=0
    g3: LineSegment StartX=264.291 StartY=-10 StartZ=0 EndX=264.291 EndY=-57 EndZ=0
    g4: LineSegment StartX=264.291 StartY=9.15 StartZ=0 EndX=264.291 EndY=-4.53021e-10 EndZ=0
    g5: LineSegment StartX=264.291 StartY=-4.53021e-10 StartZ=0 EndX=272.141 EndY=-4.53021e-10 EndZ=0
    g6: LineSegment StartX=272.141 StartY=-4.53021e-10 StartZ=0 EndX=272.141 EndY=9.15 EndZ=0
    g7: LineSegment StartX=272.141 StartY=9.15 StartZ=0 EndX=264.291 EndY=9.15 EndZ=0
  constraints (21):
    c: Coincident(g0,g1)
    c: Coincident(g1,g2)
    c: Coincident(g2,g3)
    c: Coincident(g3,g0)
    c: Horizontal(g0)
    c: Horizontal(g2)
    c: Vertical(g1)
    c: Vertical(g3)
    c: PointOnObject(g0,g-6)
    c: Coincident(g1,g-5)
    c: Coincident(g4,g5)
    c: Coincident(g5,g6)
    c: Coincident(g6,g7)
    c: Coincident(g7,g4)
    c: Vertical(g4)
    c: Vertical(g6)
    c: Horizontal(g5)
    c: Horizontal(g7)
    c: Coincident(g4,g-7)
    c: Coincident(g5,g-4)
    c: PointOnObject(g2,g-3)
FEATURE [PartDesign::Pocket] Pocket004
  BaseFeature = -> Pocket003
  Direction = (-3.683e-13,1,4.58e-13)
  Length = 0
  Length2 = 5
  Profile = -> Sketch004
  ReferenceAxis = -> Sketch004 [N_Axis]
  Refine = true
  Suppressed = false
  Type = 3
  UpToFace = -> Pocket003 [Face84]
FEATURE [PartDesign::Pad] Pad001
  BaseFeature = -> Pocket004
  Direction = (1,0,-2.77e-14)
  Length = 10
  Length2 = 10
  Profile = -> Pocket004 [Face2]
  Refine = true
  Suppressed = false
  Type = 3
  UpToFace = -> Pocket004 [Face36]
FEATURE [PartDesign::Pocket] Pocket005
  BaseFeature = -> Pad001
  Direction = (-4.71e-14,-1.577e-13,1)
  Length = 5
  Length2 = 5
  Profile = -> Pad001 [Face158]
  Refine = true
  Suppressed = false
  Type = 1
FEATURE [PartDesign::Body] Body  label="k1_motor_mount_stock_right"
  AllowCompound = false
  BaseFeature = -> Part__Feature
  Group = -> [BaseFeature,Sketch,Pocket,Sketch001,Pad,Pocket001,Sketch002,Pocket002,Sketch003,Pocket003,Sketch004,Pocket004,Pad001,Pocket005]
  Origin = -> Origin
  Placement = pos=(-200,-900,68) rot=(0,0,1;0rad)
  Tip = -> Pocket005
FEATURE [App::Part] Part  label="k1_motor_mount_stock_right_part"
  Group = -> [Part__Feature,Body,Link,Link001,Link002,Link003,Link004,Link005,Link006,Link007,Link008]
  Origin = -> Origin001
COMPONENT P5 — recipe-attached ("k1_rail_mount_right", a linked part whose construction recipe lives in a companion FreeCAD document of the same project; that document's serialized recipe follows).
Construction recipe (the companion document, serialized — sketch geometry with constraints, then the solid features built on it; lengths are millimeters unless a unit is written):

FCSTD DOCUMENT  (FreeCAD 1.0R38641 +468 (Git))
Label: k1_rail_mount
License: All rights reserved
LicenseURL: https://en.wikipedia.org/wiki/All_rights_reserved
objects: PartDesign::Pad×5, Sketcher::SketchObject×3, PartDesign::Pocket×3, PartDesign::Line×1, PartDesign::Body×1
note: 32 computed .brp shape members not serialized (recipe doc carries the construction recipe); baked Part::Feature solids carry a one-line shape summary decoded from their .brp

FEATURE [Sketcher::SketchObject] Sketch
  ArcFitTolerance = 0
  AttachmentSupport = -> [XY_Plane]
  FullyConstrained = true
  MakeInternals = false
  MapMode = 5
  sketch-geometry (4):
    g0: LineSegment StartX=-30 StartY=0 StartZ=0 EndX=30 EndY=0 EndZ=0
    g1: LineSegment StartX=30 StartY=0 StartZ=0 EndX=30 EndY=15 EndZ=0
    g2: LineSegment StartX=30 StartY=15 StartZ=0 EndX=-30 EndY=15 EndZ=0
    g3: LineSegment StartX=-30 StartY=15 StartZ=0 EndX=-30 EndY=0 EndZ=0
  constraints (11):
    c: Coincident(g0,g1)
    c: Coincident(g1,g2)
    c: Coincident(g2,g3)
    c: Coincident(g3,g0)
    c: Horizontal(g2)
    c: Vertical(g1)
    c: Vertical(g3)
    c: PointOnObject(g0,g-1)
    c: Symmetric(g0,g0,g-2)
    c: Distance(g0) = 60
    c: Distance(g1) = 15
FEATURE [PartDesign::Pad] Pad
  Direction = (0,0,1)
  Length = 8.51
  Length2 = 10
  Profile = -> Sketch
  ReferenceAxis = -> Sketch [N_Axis]
  Suppressed = false
  Type = 0
FEATURE [Sketcher::SketchObject] Sketch001
  ArcFitTolerance = 0
  AttachmentSupport = -> [Pad]
  FullyConstrained = true
  MakeInternals = false
  MapMode = 5
  Placement = pos=(0,0,8.51) rot=(0,0,1;0rad)
  sketch-geometry (1):
    g0: Circle CenterX=0 CenterY=3.5 CenterZ=0 NormalX=0 NormalY=0 NormalZ=1 AngleXU=0 Radius=1.6
  constraints (3):
    c: PointOnObject(g0,g-2)
    c: DistanceY(g-1,g0) = 3.5
    c: Radius(g0) = 1.6
FEATURE [PartDesign::Pocket] Pocket
  BaseFeature = -> Pad
  Direction = (0,0,-1)
  Length = 5
  Length2 = 5
  Profile = -> Sketch001
  ReferenceAxis = -> Sketch001 [N_Axis]
  Suppressed = false
  Type = 1
FEATURE [Sketcher::SketchObject] Sketch002
  ArcFitTolerance = 0
  AttachmentSupport = -> [Pocket]
  FullyConstrained = true
  MakeInternals = false
  MapMode = 5
  Placement = pos=(0,0,0) rot=(1,0,0;3.14159rad)
  sketch-geometry (2):
    g0: Circle CenterX=-25 CenterY=-3.7 CenterZ=0 NormalX=0 NormalY=0 NormalZ=1 AngleXU=0 Radius=2.3
    g1: Circle CenterX=25 CenterY=-3.7 CenterZ=0 NormalX=0 NormalY=0 NormalZ=1 AngleXU=0 Radius=2.3
  constraints (5):
    c: Symmetric(g1,g0,g-2)
    c: Equal(g0,g1)
    c: Radius(g0) = 2.3
    c: DistanceY(g-1,g1) = -3.7
    c: Distance(g0,g1) = 50
FEATURE [PartDesign::Pocket] Pocket001
  BaseFeature = -> Pocket
  Direction = (0,0,1)
  Length = 5.1
  Length2 = 5
  Profile = -> Sketch002
  ReferenceAxis = -> Sketch002 [N_Axis]
  Suppressed = false
  Type = 0
FEATURE [PartDesign::Line] HoleAxis_1  label="HoleAxis_frame_support"
  AttacherType = Attacher::AttachEngineLine
  AttachmentSupport = -> [Pocket001]
  Length = 4.50902
  MapMode = 19
  Placement = pos=(-2e-16,3.5,8.51) rot=(0,0,1;0rad)
  ResizeMode = 1
FEATURE [PartDesign::Pad] Pad001
  BaseFeature = -> Pocket001
  Direction = (0,-1,0)
  Length = 2.3
  Length2 = 10
  Profile = -> Pocket001 [Face1]
  Refine = true
  Suppressed = false
  Type = 0
FEATURE [PartDesign::Pocket] Pocket002
  BaseFeature = -> Pad001
  Direction = (0,-1,0)
  Length = 5.3
  Length2 = 5
  Profile = -> Pad001 [Face1]
  Suppressed = false
  Type = 0
FEATURE [PartDesign::Pad] Pad002
  BaseFeature = -> Pocket002
  Direction = (0,0,-1)
  Length = 0.15
  Length2 = 10
  Profile = -> Pocket002 [Face2]
  Refine = true
  Suppressed = false
  Type = 0
FEATURE [PartDesign::Pad] Pad003
  BaseFeature = -> Pad002
  Direction = (-1,0,0)
  Length = 70
  Length2 = 10
  Profile = -> Pad002 [Face10]
  Refine = true
  Suppressed = false
  Type = 0
FEATURE [PartDesign::Pad] Pad004
  BaseFeature = -> Pad003
  Direction = (1,0,0)
  Length = 70
  Length2 = 10
  Profile = -> Pad003 [Face3]
  Refine = true
  Suppressed = false
  Type = 0
FEATURE [PartDesign::Body] Body  label="k1_rail_mount"
  AllowCompound = false
  Group = -> [Sketch,Pad,Sketch001,Pocket,Sketch002,Pocket001,HoleAxis_1,Pad001,Pocket002,Pad002,Pad003,Pad004]
  Origin = -> Origin
  Tip = -> Pad004
COMPONENT P6 — same part as P5; its construction recipe is shown at P5.
COMPONENT P7 — recipe-attached ("k1_tensioner_left_part", a linked part whose construction recipe lives in a companion FreeCAD document of the same project; that document's serialized recipe follows).
Construction recipe (the companion document, serialized — sketch geometry with constraints, then the solid features built on it; lengths are millimeters unless a unit is written):

FCSTD DOCUMENT  (FreeCAD 1.0R38641 +678 (Git))
Label: k1_tensioner_left
License: All rights reserved
LicenseURL: https://en.wikipedia.org/wiki/All_rights_reserved
objects: PartDesign::Pocket×2, App::Link×2, Part::Feature×1, PartDesign::FeatureBase×1, Sketcher::SketchObject×1, Part::Part2DObjectPython×1, PartDesign::Body×1, App::Part×1
note: 13 computed .brp shape members not serialized (recipe doc carries the construction recipe); baked Part::Feature solids carry a one-line shape summary decoded from their .brp
EXTERNAL_REF file=cad_powge_pulley.FCStd obj=Part
EXTERNAL_REF file=cad_M4_DIN912_20mm.FCStd obj=Body

FEATURE [Part::Feature] Part__Feature  label="step"
  shape: bbox 14.4 x 34.9 x 33 mm, 57 faces (baked)
FEATURE [PartDesign::FeatureBase] BaseFeature
  BaseFeature = -> Part__Feature
  Suppressed = false
FEATURE [Sketcher::SketchObject] Sketch
  ArcFitTolerance = 1e-06
  AttachmentSupport = -> [BaseFeature]
  ExternalGeometry = -> [BaseFeature]
  FullyConstrained = true
  MakeInternals = false
  MapMode = 5
  Placement = pos=(0,-25.5,5.6e-15) rot=(0,0.707107,0.707107;3.14159rad)
  sketch-geometry (1):
    g0: Circle CenterX=-5.2 CenterY=6.7 CenterZ=0 NormalX=0 NormalY=0 NormalZ=1 AngleXU=0 Radius=0.75
  constraints (2):
    c: Coincident(g0,g-3)
    c: Diameter(g0) = 1.5
FEATURE [PartDesign::Pocket] Pocket
  BaseFeature = -> BaseFeature
  Direction = (0,-1,2e-16)
  Length = 5
  Length2 = 5
  Profile = -> Sketch
  ReferenceAxis = -> Sketch [N_Axis]
  Refine = true
  Suppressed = false
  Type = 1
FEATURE [App::Link] Link  label="cad_powge_pulley_link"
  LinkPlacement = pos=(6.7,5.2,-18.65) rot=(0,0,1;0rad)
  LinkedObject = -> <external cad_powge_pulley.FCStd>#Part
  Placement = pos=(6.7,5.2,-18.65) rot=(0,0,1;0rad)
FEATURE [App::Link] Link001  label="cad_M4_DIN912_20mm_link"
  LinkPlacement = pos=(6.7,5.2,-0.3) rot=(0,1,0;3.14159rad)
  LinkedObject = -> <external cad_M4_DIN912_20mm.FCStd>#Body
  Placement = pos=(6.7,5.2,-0.3) rot=(0,1,0;3.14159rad)
FEATURE [Part::Part2DObjectPython] ShapeString  # Draft 2D object (typed FeaturePython)
  FontFile = <path>
  Fuse = false
  Justification = 6
  JustificationReference = 0
  KeepLeftMargin = false
  MakeFace = true
  ObliqueAngle = 0
  Placement = pos=(10.15,-29.85,17) rot=(0,-1,0;4.71239rad)
  ScaleToSize = true
  Size = 5
  String = L
  Tracking = 0
FEATURE [PartDesign::Pocket] Pocket001
  BaseFeature = -> Pocket
  Direction = (-1,2e-16,4e-16)
  Length = 0.2
  Length2 = 5
  Profile = -> ShapeString
  ReferenceAxis = -> ShapeString [N_Axis]
  Refine = true
  Suppressed = false
  Type = 0
FEATURE [PartDesign::Body] Body  label="k1_tensioner_left"
  AllowCompound = false
  BaseFeature = -> Part__Feature
  Group = -> [BaseFeature,Sketch,Pocket,ShapeString,Pocket001]
  Origin = -> Origin
  Placement = pos=(0,0,0) rot=(0.57735,0.57735,0.57735;2.0944rad)
  Tip = -> Pocket001
FEATURE [App::Part] Part  label="k1_tensioner_left_part"
  Group = -> [Part__Feature,Body,Link,Link001]
  Origin = -> Origin001
note: 1 file-system path scrubbed to <path> (originals preserved in the JSON sidecar)
COMPONENT P8 — recipe-attached ("k1_tensioner_right_part", a linked part whose construction recipe lives in a companion FreeCAD document of the same project; that document's serialized recipe follows).
Construction recipe (the companion document, serialized — sketch geometry with constraints, then the solid features built on it; lengths are millimeters unless a unit is written):

FCSTD DOCUMENT  (FreeCAD 1.0R38641 +678 (Git))
Label: k1_tensioner_right
License: All rights reserved
LicenseURL: https://en.wikipedia.org/wiki/All_rights_reserved
objects: PartDesign::Pocket×11, Sketcher::SketchObject×9, PartDesign::Pad×4, PartDesign::Chamfer×3, App::Link×2, Part::Feature×1, PartDesign::FeatureBase×1, Part::Part2DObjectPython×1, PartDesign::Body×1, App::Part×1
note: 77 computed .brp shape members not serialized (recipe doc carries the construction recipe); baked Part::Feature solids carry a one-line shape summary decoded from their .brp
EXTERNAL_REF file=cad_powge_pulley.FCStd obj=Part
EXTERNAL_REF file=cad_M4_DIN912_20mm.FCStd obj=Body

FEATURE [Part::Feature] Part__Feature  label="step"
  shape: bbox 14.6 x 34.9 x 33 mm, 55 faces (baked)
FEATURE [PartDesign::FeatureBase] BaseFeature
  BaseFeature = -> Part__Feature
  Suppressed = false
FEATURE [Sketcher::SketchObject] Sketch
  ArcFitTolerance = 1e-06
  AttachmentSupport = -> [BaseFeature]
  ExternalGeometry = -> [BaseFeature]
  FullyConstrained = true
  MakeInternals = false
  MapMode = 5
  Placement = pos=(0,-10.9,0) rot=(1,0,0;1.5708rad)
  sketch-geometry (1):
    g0: Circle CenterX=5.3 CenterY=6.7 CenterZ=0 NormalX=0 NormalY=0 NormalZ=1 AngleXU=0 Radius=0.75
  constraints (2):
    c: Coincident(g0,g-3)
    c: Diameter(g0) = 1.5
FEATURE [PartDesign::Pocket] Pocket
  BaseFeature = -> BaseFeature
  Direction = (0,1,-2e-16)
  Length = 5
  Length2 = 5
  Profile = -> Sketch
  ReferenceAxis = -> Sketch [N_Axis]
  Refine = true
  Suppressed = false
  Type = 1
FEATURE [App::Link] Link  label="cad_powge_pulley_link"
  LinkPlacement = pos=(-6.7,-5.3,-27.85) rot=(0,0,1;0rad)
  LinkedObject = -> <external cad_powge_pulley.FCStd>#Part
  Placement = pos=(-6.7,-5.3,-27.85) rot=(0,0,1;0rad)
FEATURE [App::Link] Link001  label="cad_M4_DIN912_20mm_link"
  LinkPlacement = pos=(-6.7,-5.3,-34.9) rot=(0,0,1;0rad)
  LinkedObject = -> <external cad_M4_DIN912_20mm.FCStd>#Body
  Placement = pos=(-6.7,-5.3,-34.9) rot=(0,0,1;0rad)
FEATURE [Part::Part2DObjectPython] ShapeString  # Draft 2D object (typed FeaturePython)
  FontFile = <path>
  Fuse = false
  Justification = 6
  JustificationReference = 0
  KeepLeftMargin = false
  MakeFace = true
  ObliqueAngle = 0
  Placement = pos=(0.15,-9.15,14.69) rot=(0,1,0;4.71239rad)
  ScaleToSize = true
  Size = 5
  String = R
  Tracking = 0
FEATURE [PartDesign::Pocket] Pocket001
  BaseFeature = -> Pocket
  Direction = (1,0,2e-16)
  Length = 0.2
  Length2 = 5
  Profile = -> ShapeString
  ReferenceAxis = -> ShapeString [N_Axis]
  Refine = true
  Suppressed = false
  Type = 0
FEATURE [PartDesign::Pocket] Pocket002
  BaseFeature = -> Pocket001
  Direction = (1,0,0)
  Length = 1.2
  Length2 = 5
  Profile = -> Pocket001 [Face60]
  Refine = true
  Suppressed = false
  Type = 0
FEATURE [Sketcher::SketchObject] Sketch001
  ArcFitTolerance = 1e-06
  AttachmentSupport = -> [Pocket002]
  FullyConstrained = true
  MakeInternals = false
  MapMode = 5
  Placement = pos=(0.15,0,0) rot=(0.57735,-0.57735,-0.57735;2.0944rad)
  sketch-geometry (4):
    g0: LineSegment StartX=0 StartY=0 StartZ=0 EndX=36 EndY=0 EndZ=0
    g1: LineSegment StartX=36 StartY=0 StartZ=0 EndX=36 EndY=36 EndZ=0
    g2: LineSegment StartX=36 StartY=36 StartZ=0 EndX=0 EndY=36 EndZ=0
    g3: LineSegment StartX=0 StartY=36 StartZ=0 EndX=0 EndY=0 EndZ=0
  constraints (11):
    c: Coincident(g0,g1)
    c: Coincident(g1,g2)
    c: Coincident(g2,g3)
    c: Coincident(g3,g0)
    c: Horizontal(g0)
    c: Horizontal(g2)
    c: Vertical(g1)
    c: Vertical(g3)
    c: Coincident(g0,g-1)
    c: Distance(g2,g2) = 36
    c: DistanceY(g1,g1) = 36
FEATURE [PartDesign::Pocket] Pocket003
  BaseFeature = -> Pocket002
  Direction = (1,0,0)
  Length = 1.2
  Length2 = 5
  Profile = -> Sketch001
  ReferenceAxis = -> Sketch001 [N_Axis]
  Refine = true
  Suppressed = false
  Type = 0
FEATURE [PartDesign::Pad] Pad
  BaseFeature = -> Pocket003
  Direction = (-1,0,0)
  Length = 1
  Length2 = 10
  Profile = -> Pocket003 [Face8]
  Refine = true
  Suppressed = false
  Type = 0
FEATURE [PartDesign::Pad] Pad001
  BaseFeature = -> Pad
  Direction = (-1,0,0)
  Length = 1
  Length2 = 10
  Profile = -> Pad [Face45]
  Refine = true
  Suppressed = false
  Type = 0
FEATURE [PartDesign::Chamfer] Chamfer
  Angle = 45
  Base = -> Pad001 [Edge31,Edge29]
  BaseFeature = -> Pad001
  ChamferType = 0
  FlipDirection = false
  Refine = true
  Size = 0.8
  Size2 = 1
  SupportTransform = false
  Suppressed = false
  UseAllEdges = false
FEATURE [PartDesign::Pocket] Pocket004
  BaseFeature = -> Chamfer
  Direction = (1,0,0)
  Length = 0.2
  Length2 = 5
  Profile = -> Chamfer [Face56,Face57]
  Refine = true
  Suppressed = false
  Type = 0
FEATURE [Sketcher::SketchObject] Sketch002
  ArcFitTolerance = 1e-06
  AttachmentSupport = -> [Pocket004]
  ExternalGeometry = -> [Pocket004]
  FullyConstrained = true
  MakeInternals = false
  MapMode = 5
  Placement = pos=(0,-0.1,0) rot=(0,0.707107,0.707107;3.14159rad)
  sketch-geometry (4):
    g0: LineSegment StartX=-9 StartY=3.26 StartZ=0 EndX=-9 EndY=33 EndZ=0
    g1: LineSegment StartX=-9 StartY=33 StartZ=0 EndX=-10.35 EndY=33 EndZ=0
    g2: LineSegment StartX=-10.35 StartY=33 StartZ=0 EndX=-10.35 EndY=4.61 EndZ=0
    g3: LineSegment StartX=-9 StartY=3.26 StartZ=0 EndX=-10.35 EndY=4.61 EndZ=0
  constraints (11):
    c: PointOnObject(g0,g-5)
    c: PointOnObject(g0,g-6)
    c: Vertical(g0)
    c: Coincident(g1,g0)
    c: Coincident(g1,g-4)
    c: Coincident(g2,g1)
    c: Vertical(g2)
    c: Coincident(g3,g0)
    c: Coincident(g3,g2)
    c: Parallel(g3,g-5)
    c: Distance(g1,g1) = 1.35
FEATURE [PartDesign::Pad] Pad002
  BaseFeature = -> Pocket004
  Direction = (0,1,-2e-16)
  Length = 10
  Length2 = 10
  Profile = -> Sketch002
  ReferenceAxis = -> Sketch002 [N_Axis]
  Refine = true
  Suppressed = false
  Type = 3
  UpToFace = -> Pocket004 [Face11]
FEATURE [Sketcher::SketchObject] Sketch003
  ArcFitTolerance = 1e-06
  AttachmentSupport = -> [Pad002]
  ExternalGeometry = -> [Pad002]
  FullyConstrained = true
  MakeInternals = false
  MapMode = 5
  Placement = pos=(-1.12e-14,-35,0) rot=(1,0,0;1.5708rad)
  sketch-geometry (4):
    g0: LineSegment StartX=9.05 StartY=3.31 StartZ=0 EndX=9.05 EndY=33 EndZ=0
    g1: LineSegment StartX=9.05 StartY=33 StartZ=0 EndX=10.35 EndY=33 EndZ=0
    g2: LineSegment StartX=10.35 StartY=33 StartZ=0 EndX=10.35 EndY=4.61 EndZ=0
    g3: LineSegment StartX=9.05 StartY=3.31 StartZ=0 EndX=10.35 EndY=4.61 EndZ=0
  constraints (11):
    c: PointOnObject(g0,g-5)
    c: PointOnObject(g0,g-3)
    c: Vertical(g0)
    c: Coincident(g1,g0)
    c: Coincident(g1,g-6)
    c: Coincident(g2,g1)
    c: Vertical(g2)
    c: Coincident(g3,g0)
    c: Coincident(g3,g2)
    c: Parallel(g3,g-5)
    c: Distance(g1,g1) = 1.3
FEATURE [PartDesign::Pad] Pad003
  BaseFeature = -> Pad002
  Direction = (0,-1,2e-16)
  Length = 10
  Length2 = 10
  Profile = -> Sketch003
  ReferenceAxis = -> Sketch003 [N_Axis]
  Refine = true
  Suppressed = false
  Type = 3
  UpToFace = -> Pad002 [Face9]
FEATURE [Sketcher::SketchObject] Sketch004
  ArcFitTolerance = 1e-06
  AttachmentSupport = -> [Pad003]
  ExternalGeometry = -> [Pad003]
  FullyConstrained = true
  MakeInternals = false
  MapMode = 5
  Placement = pos=(10.35,0,0) rot=(0.57735,0.57735,0.57735;2.0944rad)
  sketch-geometry (8):
    g0: LineSegment StartX=-16.45 StartY=33 StartZ=0 EndX=-16.45 EndY=0 EndZ=0
    g1: LineSegment StartX=-16.45 StartY=0 StartZ=0 EndX=-0.1 EndY=0 EndZ=0
    g2: LineSegment StartX=-0.1 StartY=0 StartZ=0 EndX=-0.1 EndY=33 EndZ=0
    g3: LineSegment StartX=-0.1 StartY=33 StartZ=0 EndX=-16.45 EndY=33 EndZ=0
    g4: LineSegment StartX=-28.3 StartY=33 StartZ=0 EndX=-35 EndY=33 EndZ=0
    g5: LineSegment StartX=-35 StartY=33 StartZ=0 EndX=-35 EndY=0 EndZ=0
    g6: LineSegment StartX=-35 StartY=0 StartZ=0 EndX=-28.3 EndY=0 EndZ=0
    g7: LineSegment StartX=-28.3 StartY=0 StartZ=0 EndX=-28.3 EndY=33 EndZ=0
  constraints (20):
    c: Coincident(g0,g1)
    c: Coincident(g1,g2)
    c: Coincident(g2,g3)
    c: Coincident(g3,g0)
    c: Vertical(g0)
    c: Vertical(g2)
    c: Horizontal(g1)
    c: Coincident(g0,g-3)
    c: PointOnObject(g1,g-1)
    c: Coincident(g2,g-3)
    c: Coincident(g4,g5)
    c: Coincident(g5,g6)
    c: Coincident(g6,g7)
    c: Coincident(g7,g4)
    c: Horizontal(g6)
    c: Vertical(g5)
    c: Vertical(g7)
    c: Coincident(g4,g-4)
    c: PointOnObject(g5,g-1)
    c: Coincident(g4,g-4)
FEATURE [PartDesign::Pocket] Pocket005
  BaseFeature = -> Pad003
  Direction = (-1,0,0)
  Length = 0.1
  Length2 = 5
  Profile = -> Sketch004
  ReferenceAxis = -> Sketch004 [N_Axis]
  Refine = true
  Suppressed = false
  Type = 0
FEATURE [PartDesign::Pocket] Pocket006
  BaseFeature = -> Pocket005
  Direction = (-1,0,0)
  Length = 0
  Length2 = 5
  Profile = -> Pocket005 [Face55]
  Refine = true
  Suppressed = false
  Type = 3
  UpToFace = -> Pocket005 [Face17]
FEATURE [Sketcher::SketchObject] Sketch005
  ArcFitTolerance = 1e-06
  AttachmentSupport = -> [Pocket006]
  ExternalGeometry = -> [Pocket006]
  FullyConstrained = true
  MakeInternals = false
  MapMode = 5
  Placement = pos=(1.1168,1.5794,-1.1168) rot=(0.122253,0.881412,0.456253;2.67774rad)
  sketch-geometry (4):
    g0: LineSegment StartX=-9.10273 StartY=3.5278 StartZ=0 EndX=-9.75593 EndY=2.60404 EndZ=0
    g1: LineSegment StartX=-9.10273 StartY=3.5278 StartZ=0 EndX=-7.9678 EndY=2.72529 EndZ=0
    g2: LineSegment StartX=-7.9678 StartY=2.72529 StartZ=0 EndX=-8.621 EndY=1.80153 EndZ=0
    g3: LineSegment StartX=-8.621 StartY=1.80153 StartZ=0 EndX=-9.75593 EndY=2.60404 EndZ=0
  constraints (11):
    c: Coincident(g0,g-3)
    c: Coincident(g1,g-3)
    c: PointOnObject(g1,g-3)
    c: Coincident(g2,g1)
    c: PointOnObject(g2,g-4)
    c: Coincident(g3,g2)
    c: Coincident(g3,g0)
    c: Perpendicular(g-3,g0)
    c: Perpendicular(g-3,g2)
    c: PointOnObject(g0,g-4)
    c: Distance(g1,g1) = 1.39
FEATURE [PartDesign::Pocket] Pocket007
  BaseFeature = -> Pocket006
  Direction = (-0.5,-0.707107,0.5)
  Length = 5
  Length2 = 5
  Profile = -> Sketch005
  ReferenceAxis = -> Sketch005 [N_Axis]
  Refine = true
  Reversed = true
  Suppressed = false
  Type = 0
FEATURE [PartDesign::Chamfer] Chamfer001
  Angle = 45
  Base = -> Pocket007 [Edge79,Edge86,Edge78]
  BaseFeature = -> Pocket007
  ChamferType = 0
  FlipDirection = false
  Refine = true
  Size = 0.8
  Size2 = 1
  SupportTransform = false
  Suppressed = false
  UseAllEdges = false
FEATURE [Sketcher::SketchObject] Sketch006
  ArcFitTolerance = 1e-06
  AttachmentSupport = -> [Chamfer001]
  ExternalGeometry = -> [Chamfer001]
  FullyConstrained = true
  MakeInternals = false
  MapMode = 5
  Placement = pos=(13.5265,-19.1294,-13.5265) rot=(0.957372,0.132788,0.256527;2.22139rad)
  sketch-geometry (4):
    g0: LineSegment StartX=-5.16905 StartY=23.8336 StartZ=0 EndX=-4.51585 EndY=22.9099 EndZ=0
    g1: LineSegment StartX=-4.51585 StartY=22.9099 StartZ=0 EndX=-5.5528 EndY=22.1766 EndZ=0
    g2: LineSegment StartX=-5.5528 StartY=22.1766 StartZ=0 EndX=-6.206 EndY=23.1004 EndZ=0
    g3: LineSegment StartX=-6.206 StartY=23.1004 StartZ=0 EndX=-5.16905 EndY=23.8336 EndZ=0
  constraints (11):
    c: Coincident(g0,g-3)
    c: Coincident(g1,g0)
    c: PointOnObject(g1,g-4)
    c: Coincident(g2,g1)
    c: PointOnObject(g2,g-3)
    c: Coincident(g3,g2)
    c: Coincident(g3,g0)
    c: PointOnObject(g0,g-4)
    c: Perpendicular(g0,g3)
    c: Perpendicular(g3,g2)
    c: Distance(g3,g3) = 1.27
FEATURE [PartDesign::Pocket] Pocket008
  BaseFeature = -> Chamfer001
  Direction = (-0.5,0.707107,0.5)
  Length = 5
  Length2 = 5
  Profile = -> Sketch006
  ReferenceAxis = -> Sketch006 [N_Axis]
  Refine = true
  Reversed = true
  Suppressed = false
  Type = 0
FEATURE [PartDesign::Chamfer] Chamfer002
  Angle = 45
  Base = -> Pocket008 [Edge79,Edge68,Edge69]
  BaseFeature = -> Pocket008
  ChamferType = 0
  FlipDirection = false
  Refine = true
  Size = 0.8
  Size2 = 1
  SupportTransform = false
  Suppressed = false
  UseAllEdges = false
FEATURE [Sketcher::SketchObject] Sketch007
  ArcFitTolerance = 1e-06
  AttachmentSupport = -> [Chamfer002]
  ExternalGeometry = -> [Chamfer002]
  FullyConstrained = true
  MakeInternals = false
  MapMode = 5
  Placement = pos=(1.1168,1.5794,-1.1168) rot=(0.122253,0.881412,0.456253;2.67774rad)
  sketch-geometry (4):
    g0: LineSegment StartX=-9.89291 StartY=2.7009 StartZ=0 EndX=-9.23971 EndY=3.62466 EndZ=0
    g1: LineSegment StartX=-9.23971 StartY=3.62466 StartZ=0 EndX=-8.69266 EndY=3.23784 EndZ=0
    g2: LineSegment StartX=-8.69266 StartY=3.23784 StartZ=0 EndX=-9.34586 EndY=2.31408 EndZ=0
    g3: LineSegment StartX=-9.34586 StartY=2.31408 StartZ=0 EndX=-9.89291 EndY=2.7009 EndZ=0
  constraints (10):
    c: Coincident(g0,g-7)
    c: Coincident(g0,g-7)
    c: Coincident(g1,g-7)
    c: PointOnObject(g1,g-5)
    c: Coincident(g2,g1)
    c: PointOnObject(g2,g-4)
    c: Coincident(g3,g2)
    c: Coincident(g3,g-7)
    c: Distance(g1,g1) = 0.67
    c: Perpendicular(g3,g2)
FEATURE [PartDesign::Pocket] Pocket009
  BaseFeature = -> Chamfer002
  Direction = (-0.5,-0.707107,0.5)
  Length = 5
  Length2 = 5
  Profile = -> Sketch007
  ReferenceAxis = -> Sketch007 [N_Axis]
  Refine = true
  Reversed = true
  Suppressed = false
  Type = 0
FEATURE [Sketcher::SketchObject] Sketch008
  ArcFitTolerance = 1e-06
  AttachmentSupport = -> [Pocket009]
  ExternalGeometry = -> [Pocket009]
  FullyConstrained = true
  MakeInternals = false
  MapMode = 5
  Placement = pos=(13.5265,-19.1294,-13.5265) rot=(0.957372,0.132788,0.256527;2.22139rad)
  sketch-geometry (4):
    g0: LineSegment StartX=-4.4366 StartY=22.9659 StartZ=0 EndX=-5.0898 EndY=23.8897 EndZ=0
    g1: LineSegment StartX=-5.0898 StartY=23.8897 StartZ=0 EndX=-5.76749 EndY=23.4105 EndZ=0
    g2: LineSegment StartX=-4.4366 StartY=22.9659 StartZ=0 EndX=-5.1143 EndY=22.4867 EndZ=0
    g3: LineSegment StartX=-5.1143 StartY=22.4867 StartZ=0 EndX=-5.76749 EndY=23.4105 EndZ=0
  constraints (10):
    c: Coincident(g0,g-3)
    c: Coincident(g0,g-3)
    c: Coincident(g1,g0)
    c: PointOnObject(g1,g-5)
    c: Coincident(g2,g-3)
    c: PointOnObject(g2,g-4)
    c: Coincident(g3,g2)
    c: Coincident(g3,g1)
    c: Perpendicular(g3,g1)
    c: Distance(g1,g1) = 0.83
FEATURE [PartDesign::Pocket] Pocket010
  BaseFeature = -> Pocket009
  Direction = (-0.5,0.707107,0.5)
  Length = 5
  Length2 = 5
  Profile = -> Sketch008
  ReferenceAxis = -> Sketch008 [N_Axis]
  Refine = true
  Reversed = true
  Suppressed = false
  Type = 0
FEATURE [PartDesign::Body] Body  label="k1_tensioner_right"
  AllowCompound = false
  BaseFeature = -> Part__Feature
  Group = -> [BaseFeature,Sketch,Pocket,ShapeString,Pocket001,Pocket002,Sketch001,Pocket003,Pad,Pad001,Chamfer,Pocket004,Sketch002,Pad002,Sketch003,Pad003,Sketch004,Pocket005,Pocket006,Sketch005,Pocket007,Chamfer001,Sketch006,Pocket008,Chamfer002,Sketch007,Pocket009,Sketch008,Pocket010]
  Origin = -> Origin
  Placement = pos=(0,0,0) rot=(0.57735,-0.57735,-0.57735;2.0944rad)
  Tip = -> Pocket010
FEATURE [App::Part] Part  label="k1_tensioner_right_part"
  Group = -> [Part__Feature,Body,Link,Link001]
  Origin = -> Origin001
note: 1 file-system path scrubbed to <path> (originals preserved in the JSON sidecar)
COMPONENT P9 — recipe-attached ("k1_toolhead_part", a linked part whose construction recipe lives in a companion FreeCAD document of the same project; that document's serialized recipe follows).
Construction recipe (the companion document, serialized — sketch geometry with constraints, then the solid features built on it; lengths are millimeters unless a unit is written):

FCSTD DOCUMENT  (FreeCAD 1.0R38641 +468 (Git))
Label: k1_toolhead
License: All rights reserved
LicenseURL: https://en.wikipedia.org/wiki/All_rights_reserved
objects: Sketcher::SketchObject×12, PartDesign::Pocket×10, App::Link×9, PartDesign::Pad×9, PartDesign::Fillet×2, PartDesign::Line×2, Part::Feature×1, PartDesign::FeatureBase×1, PartDesign::Body×1, App::Part×1
note: 93 computed .brp shape members not serialized (recipe doc carries the construction recipe); baked Part::Feature solids carry a one-line shape summary decoded from their .brp
EXTERNAL_REF file=k1_toolhead_left_clamp.FCStd obj=Part
EXTERNAL_REF file=k1_toolhead_right_clamp.FCStd obj=Part
EXTERNAL_REF file=k1_toolhead_spacer.FCStd obj=Part
EXTERNAL_REF file=cad_hotend.FCStd obj=K1_Hotend
EXTERNAL_REF file=cad_mgn9h_block.FCStd obj=Body
EXTERNAL_REF file=cad_extruder.FCStd obj=K1_Extruder_Assembly_v25
EXTERNAL_REF file=k1_toolhead_cover.FCStd obj=Part
EXTERNAL_REF file=cad_3010.FCStd obj=DC_fan_3010_v3
EXTERNAL_REF file=cad_pcb.FCStd obj=COMPOUND069

FEATURE [Part::Feature] Part__Feature  label="step"
  shape: bbox 62.42 x 48.4 x 81 mm, 177 faces (baked)
FEATURE [PartDesign::FeatureBase] BaseFeature
  BaseFeature = -> Part__Feature
  Suppressed = false
FEATURE [App::Link] Link  label="k1_toolhead_left_clamp_link"
  LinkPlacement = pos=(29.25,-15.3795,18.9) rot=(0.57735,-0.57735,-0.57735;2.0944rad)
  LinkedObject = -> <external k1_toolhead_left_clamp.FCStd>#Part
  Placement = pos=(29.25,-15.3795,18.9) rot=(0.57735,-0.57735,-0.57735;2.0944rad)
FEATURE [App::Link] Link001  label="k1_toolhead_right_clamp_link"
  LinkPlacement = pos=(29.25,33.2,18.9) rot=(0.57735,-0.57735,-0.57735;2.0944rad)
  LinkedObject = -> <external k1_toolhead_right_clamp.FCStd>#Part
  Placement = pos=(29.25,33.2,18.9) rot=(0.57735,-0.57735,-0.57735;2.0944rad)
FEATURE [App::Link] Link002  label="k1_toolhead_spacer_link"
  LinkPlacement = pos=(26.3,-3.8445e-07,31.75) rot=(0.57735,-0.57735,-0.57735;2.0944rad)
  LinkedObject = -> <external k1_toolhead_spacer.FCStd>#Part
  Placement = pos=(26.3,-3.8445e-07,31.75) rot=(0.57735,-0.57735,-0.57735;2.0944rad)
FEATURE [App::Link] Link003  label="k1 hotend_link"
  LinkPlacement = pos=(0,-0.2,0) rot=(0,0,1;0rad)
  LinkedObject = -> <external cad_hotend.FCStd>#K1_Hotend
  Placement = pos=(0,-0.2,0) rot=(0,0,1;0rad)
FEATURE [App::Link] Link004  label="cad_mgn9h_block_link"
  LinkPlacement = pos=(-0.49,3.6e-15,23.1) rot=(0,0,1;1.5708rad)
  LinkedObject = -> <external cad_mgn9h_block.FCStd>#Body
  Placement = pos=(-0.49,3.6e-15,23.1) rot=(0,0,1;1.5708rad)
FEATURE [App::Link] Link005  label="cad_extruder_link"
  LinkPlacement = pos=(2.3,0.3,54.5) rot=(0,0,1;1.5708rad)
  LinkedObject = -> <external cad_extruder.FCStd>#K1_Extruder_Assembly_v25
  Placement = pos=(2.3,0.3,54.5) rot=(0,0,1;1.5708rad)
FEATURE [App::Link] Link006  label="k1_toolhead_cover_link"
  LinkPlacement = pos=(119.56,-251.103,-19.75) rot=(0,0,1;1.5708rad)
  LinkedObject = -> <external k1_toolhead_cover.FCStd>#Part
  Placement = pos=(119.56,-251.103,-19.75) rot=(0,0,1;1.5708rad)
FEATURE [Sketcher::SketchObject] Sketch
  ArcFitTolerance = 1e-06
  AttachmentSupport = -> [BaseFeature]
  ExternalGeometry = -> [BaseFeature]
  FullyConstrained = true
  MakeInternals = false
  MapMode = 5
  Placement = pos=(0,0,34.1) rot=(0,0,1;0rad)
  sketch-geometry (4):
    g0: ArcOfCircle CenterX=15.6 CenterY=-2e-16 CenterZ=0 NormalX=0 NormalY=0 NormalZ=1 AngleXU=0 Radius=2.1 StartAngle=4.71239 EndAngle=7.85398
    g1: ArcOfCircle CenterX=16 CenterY=0 CenterZ=0 NormalX=0 NormalY=0 NormalZ=1 AngleXU=0 Radius=2.1 StartAngle=4.71239 EndAngle=7.85398
    g2: LineSegment StartX=15.6 StartY=2.1 StartZ=0 EndX=16 EndY=2.1 EndZ=0
    g3: LineSegment StartX=16 StartY=-2.1 StartZ=0 EndX=15.6 EndY=-2.1 EndZ=0
  constraints (9):
    c: Coincident(g0,g-3)
    c: Coincident(g0,g-3)
    c: Coincident(g1,g-4)
    c: Coincident(g1,g-4)
    c: Tangent(g2,g0) = 1.5708
    c: Coincident(g2,g1)
    c: Coincident(g3,g1)
    c: Coincident(g3,g0)
    c: Horizontal(g3)
FEATURE [PartDesign::Pad] Pad
  BaseFeature = -> BaseFeature
  Direction = (0,0,1)
  Length = 10
  Length2 = 10
  Profile = -> Sketch
  ReferenceAxis = -> Sketch [N_Axis]
  Refine = true
  Reversed = true
  Suppressed = false
  Type = 3
  UpToFace = -> BaseFeature [Face148]
FEATURE [PartDesign::Fillet] Fillet
  Base = -> Pad [Edge424]
  BaseFeature = -> Pad
  Radius = 3
  Refine = true
  SupportTransform = false
  Suppressed = false
  UseAllEdges = false
FEATURE [PartDesign::Pad] Pad001
  BaseFeature = -> Fillet
  Direction = (0,0,1)
  Length = 1
  Length2 = 10
  Profile = -> Fillet [Face7]
  Refine = true
  Suppressed = false
  Type = 0
FEATURE [PartDesign::Pad] Pad002
  BaseFeature = -> Pad001
  Direction = (0,0,1)
  Length = 1
  Length2 = 10
  Profile = -> Pad001 [Face143,Face146,Face145,Face144]
  Refine = true
  Suppressed = false
  Type = 0
FEATURE [PartDesign::Line] DatumLine
  AttacherType = Attacher::AttachEngineLine
  AttachmentOffset = pos=(0,1,0) rot=(0,0,1;0rad)
  AttachmentSupport = -> [Pad002]
  Length = 20
  MapMode = 19
  Placement = pos=(5.5,23.2,45.4) rot=(0,0.707107,0.707107;3.14159rad)
  ResizeMode = 0
FEATURE [PartDesign::Line] DatumLine001
  AttacherType = Attacher::AttachEngineLine
  AttachmentOffset = pos=(0,1,0) rot=(0,0,1;0rad)
  AttachmentSupport = -> [Pad002]
  Length = 20
  MapMode = 19
  Placement = pos=(5.5,23.2,65.4) rot=(1,0,0;1.5708rad)
  ResizeMode = 0
FEATURE [PartDesign::Pad] Pad003
  BaseFeature = -> Pad002
  Direction = (2e-16,1,-2e-16)
  Length = 1
  Length2 = 10
  Profile = -> Pad002 [Face149,Face148]
  Refine = true
  Suppressed = false
  Type = 0
FEATURE [PartDesign::Pad] Pad004
  BaseFeature = -> Pad003
  Direction = (0,-1,0)
  Length = 10
  Length2 = 10
  Profile = -> Pad003 [Face146]
  Refine = true
  Suppressed = false
  Type = 3
  UpToFace = -> Pad003 [Face23]
FEATURE [PartDesign::Pad] Pad005
  BaseFeature = -> Pad004
  Direction = (0,1,0)
  Length = 10
  Length2 = 10
  Profile = -> Pad004 [Edge488]
  Refine = true
  Suppressed = false
  Type = 3
  UpToFace = -> Pad004 [Face52]
FEATURE [PartDesign::Pad] Pad006
  BaseFeature = -> Pad005
  Direction = (0,1,0)
  Length = 10
  Length2 = 10
  Profile = -> Pad005 [Edge45]
  Refine = true
  Suppressed = false
  Type = 3
  UpToFace = -> Pad005 [Face44]
FEATURE [PartDesign::Pad] Pad007
  BaseFeature = -> Pad006
  Direction = (-1.4e-15,1,0)
  Length = 10
  Length2 = 10
  Profile = -> Pad006 [Edge480]
  Refine = true
  Suppressed = false
  Type = 3
  UpToFace = -> Pad006 [Face167]
FEATURE [Sketcher::SketchObject] Sketch001
  ArcFitTolerance = 1e-06
  AttachmentSupport = -> [Pad007]
  ExternalGeometry = -> [DatumLine001,DatumLine]
  FullyConstrained = true
  MakeInternals = false
  MapMode = 5
  Placement = pos=(0,24.2,0) rot=(0,0.707107,0.707107;3.14159rad)
  sketch-geometry (2):
    g0: Circle CenterX=-5.5 CenterY=65.4 CenterZ=0 NormalX=0 NormalY=0 NormalZ=1 AngleXU=0 Radius=1.55
    g1: Circle CenterX=-5.5 CenterY=45.4 CenterZ=0 NormalX=0 NormalY=0 NormalZ=1 AngleXU=0 Radius=1.55
  constraints (4):
    c: Coincident(g0,g-3)
    c: Coincident(g1,g-4)
    c: Equal(g1,g0)
    c: Diameter(g0) = 3.1
FEATURE [PartDesign::Pocket] Pocket
  BaseFeature = -> Pad007
  Direction = (0,-1,2e-16)
  Length = 5
  Length2 = 5
  Profile = -> Sketch001
  ReferenceAxis = -> Sketch001 [N_Axis]
  Refine = true
  Suppressed = false
  Type = 0
FEATURE [Sketcher::SketchObject] Sketch002
  ArcFitTolerance = 1e-06
  AttachmentSupport = -> [Pocket]
  ExternalGeometry = -> [DatumLine]
  FullyConstrained = true
  MakeInternals = false
  MapMode = 5
  Placement = pos=(0,-24.2,0) rot=(1,0,0;1.5708rad)
  sketch-geometry (1):
    g0: Circle CenterX=5.5 CenterY=45.4 CenterZ=0 NormalX=0 NormalY=0 NormalZ=1 AngleXU=0 Radius=1.55
  constraints (2):
    c: Coincident(g0,g-3)
    c: Diameter(g0) = 3.1
FEATURE [PartDesign::Pocket] Pocket001
  BaseFeature = -> Pocket
  Direction = (0,1,-2e-16)
  Length = 5
  Length2 = 5
  Profile = -> Sketch002
  ReferenceAxis = -> Sketch002 [N_Axis]
  Refine = true
  Suppressed = false
  Type = 0
FEATURE [Sketcher::SketchObject] Sketch003
  ArcFitTolerance = 1e-06
  AttachmentSupport = -> [Pocket001]
  ExternalGeometry = -> [DatumLine001,DatumLine]
  FullyConstrained = true
  MakeInternals = false
  MapMode = 5
  Placement = pos=(0,24.2,0) rot=(0,0.707107,0.707107;3.14159rad)
  sketch-geometry (2):
    g0: Circle CenterX=-5.5 CenterY=65.4 CenterZ=0 NormalX=0 NormalY=0 NormalZ=1 AngleXU=0 Radius=3.1
    g1: Circle CenterX=-5.5 CenterY=45.4 CenterZ=0 NormalX=0 NormalY=0 NormalZ=1 AngleXU=0 Radius=3.1
  constraints (4):
    c: Coincident(g0,g-3)
    c: Coincident(g1,g-4)
    c: Equal(g1,g0)
    c: Diameter(g0) = 6.2
FEATURE [PartDesign::Pocket] Pocket002
  BaseFeature = -> Pocket001
  Direction = (0,-1,2e-16)
  Length = 1
  Length2 = 5
  Profile = -> Sketch003
  ReferenceAxis = -> Sketch003 [N_Axis]
  Refine = true
  Suppressed = false
  Type = 0
FEATURE [Sketcher::SketchObject] Sketch004
  ArcFitTolerance = 1e-06
  AttachmentSupport = -> [Pocket002]
  ExternalGeometry = -> [DatumLine]
  FullyConstrained = true
  MakeInternals = false
  MapMode = 5
  Placement = pos=(0,-24.2,0) rot=(1,0,0;1.5708rad)
  sketch-geometry (1):
    g0: Circle CenterX=5.5 CenterY=45.4 CenterZ=0 NormalX=0 NormalY=0 NormalZ=1 AngleXU=0 Radius=3.1
  constraints (2):
    c: Coincident(g0,g-3)
    c: Diameter(g0) = 6.2
FEATURE [PartDesign::Pocket] Pocket003
  BaseFeature = -> Pocket002
  Direction = (0,1,-2e-16)
  Length = 1
  Length2 = 5
  Profile = -> Sketch004
  ReferenceAxis = -> Sketch004 [N_Axis]
  Refine = true
  Suppressed = false
  Type = 0
FEATURE [Sketcher::SketchObject] Sketch005
  ArcFitTolerance = 1e-06
  AttachmentSupport = -> [Pocket003]
  ExternalGeometry = -> [Pocket003]
  FullyConstrained = true
  MakeInternals = false
  MapMode = 5
  Placement = pos=(0,13.9,0) rot=(0,0.707107,0.707107;3.14159rad)
  sketch-geometry (3):
    g0: LineSegment StartX=14.38 StartY=29.3 StartZ=0 EndX=10.88 EndY=35.1 EndZ=0
    g1: LineSegment StartX=14.38 StartY=29.3 StartZ=0 EndX=14.38 EndY=35.1 EndZ=0
    g2: LineSegment StartX=14.38 StartY=35.1 StartZ=0 EndX=10.88 EndY=35.1 EndZ=0
  constraints (8):
    c: PointOnObject(g0,g-3)
    c: PointOnObject(g0,g-5)
    c: Coincident(g1,g-4)
    c: Coincident(g2,g1)
    c: Coincident(g2,g0)
    c: Coincident(g1,g0)
    c: Distance(g2,g2) = 3.5
    c: Distance(g1,g1) = 5.8
FEATURE [PartDesign::Pocket] Pocket004
  BaseFeature = -> Pocket003
  Direction = (0,-1,2e-16)
  Length = 0
  Length2 = 5
  Profile = -> Sketch005
  ReferenceAxis = -> Sketch005 [N_Axis]
  Refine = true
  Reversed = true
  Suppressed = false
  Type = 3
  UpToFace = -> Pocket003 [Face61]
FEATURE [PartDesign::Fillet] Fillet001
  Base = -> Pocket004 [Edge452]
  BaseFeature = -> Pocket004
  Radius = 3
  Refine = true
  SupportTransform = false
  Suppressed = false
  UseAllEdges = false
FEATURE [App::Link] Link007  label="cad_3010_link"
  LinkPlacement = pos=(2.84,-387,-65.5) rot=(0,0,1;0rad)
  LinkedObject = -> <external cad_3010.FCStd>#DC_fan_3010_v3
  Placement = pos=(2.84,-387,-65.5) rot=(0,0,1;0rad)
FEATURE [App::Link] Link008  label="cad_pcb_link"
  LinkPlacement = pos=(3,0,0) rot=(0,0,1;0rad)
  LinkedObject = -> <external cad_pcb.FCStd>#COMPOUND069
  Placement = pos=(3,0,0) rot=(0,0,1;0rad)
FEATURE [Sketcher::SketchObject] Sketch006
  ArcFitTolerance = 1e-06
  AttachmentSupport = -> [Fillet001]
  ExternalGeometry = -> [Fillet001]
  FullyConstrained = true
  MakeInternals = false
  MapMode = 5
  Placement = pos=(0,-24.2,0) rot=(1,0,0;1.5708rad)
  sketch-geometry (5):
    g0: LineSegment StartX=-3.72819 StartY=35.1 StartZ=0 EndX=-14.88 EndY=35.1 EndZ=0
    g1: LineSegment StartX=-14.88 StartY=35.1 StartZ=0 EndX=-17.38 EndY=30.4377 EndZ=0
    g2: LineSegment StartX=-17.38 StartY=30.4377 StartZ=0 EndX=-17.38 EndY=59.5597 EndZ=0
    g3: LineSegment StartX=-17.38 StartY=59.5597 StartZ=0 EndX=-3.72819 EndY=59.5597 EndZ=0
    g4: LineSegment StartX=-3.72819 StartY=59.5597 StartZ=0 EndX=-3.72819 EndY=35.1 EndZ=0
  constraints (15):
    c: PointOnObject(g0,g-5)
    c: PointOnObject(g0,g-5)
    c: Coincident(g1,g0)
    c: PointOnObject(g1,g-4)
    c: Coincident(g2,g1)
    c: Vertical(g2)
    c: Coincident(g3,g2)
    c: Horizontal(g3)
    c: Parallel(g-6,g1)
    c: Distance(g0,g2) = 2.5
    c: PointOnObject(g3,g-6)
    c: Coincident(g4,g3)
    c: Coincident(g4,g0)
    c: Vertical(g4)
    c: Distance(g-6,g4) = 4
FEATURE [PartDesign::Pocket] Pocket005
  BaseFeature = -> Fillet001
  Direction = (0,1,-2e-16)
  Length = 5
  Length2 = 5
  Profile = -> Sketch006
  ReferenceAxis = -> Sketch006 [N_Axis]
  Refine = true
  Suppressed = false
  Type = 1
FEATURE [Sketcher::SketchObject] Sketch007
  ArcFitTolerance = 1e-06
  AttachmentSupport = -> [Pocket005]
  ExternalGeometry = -> [Pocket005]
  FullyConstrained = true
  MakeInternals = false
  MapMode = 5
  Placement = pos=(0,-24.2,0) rot=(1,0,0;1.5708rad)
  sketch-geometry (4):
    g0: LineSegment StartX=-3.72819 StartY=35.1 StartZ=0 EndX=-17.38 EndY=35.1 EndZ=0
    g1: LineSegment StartX=-17.38 StartY=35.1 StartZ=0 EndX=-17.38 EndY=33.1 EndZ=0
    g2: LineSegment StartX=-17.38 StartY=33.1 StartZ=0 EndX=-3.72819 EndY=33.1 EndZ=0
    g3: LineSegment StartX=-3.72819 StartY=33.1 StartZ=0 EndX=-3.72819 EndY=35.1 EndZ=0
  constraints (11):
    c: Coincident(g0,g1)
    c: Coincident(g1,g2)
    c: Coincident(g2,g3)
    c: Coincident(g3,g0)
    c: Horizontal(g0)
    c: Horizontal(g2)
    c: Vertical(g1)
    c: Vertical(g3)
    c: Coincident(g0,g-3)
    c: PointOnObject(g1,g-4)
    c: Distance(g1,g1) = 2
FEATURE [PartDesign::Pocket] Pocket006
  BaseFeature = -> Pocket005
  Direction = (0,1,-2e-16)
  Length = 10
  Length2 = 5
  Profile = -> Sketch007
  ReferenceAxis = -> Sketch007 [N_Axis]
  Refine = true
  Suppressed = false
  Type = 0
FEATURE [Sketcher::SketchObject] Sketch008
  ArcFitTolerance = 1e-06
  AttachmentSupport = -> [Pocket006]
  ExternalGeometry = -> [Pocket006]
  FullyConstrained = true
  MakeInternals = false
  MapMode = 5
  Placement = pos=(0,24.2,0) rot=(0,0.707107,0.707107;3.14159rad)
  sketch-geometry (7):
    g0: LineSegment StartX=-8.00184 StartY=70.44 StartZ=0 EndX=-2.10592 EndY=70.44 EndZ=0
    g1: LineSegment StartX=0.811065 StartY=65 StartZ=0 EndX=-2.10592 EndY=70.44 EndZ=0
    g2: LineSegment StartX=-13.4418 StartY=65 StartZ=0 EndX=-8.00184 EndY=70.44 EndZ=0
    g3: LineSegment StartX=-13.4418 StartY=65 StartZ=0 EndX=-9.21183 EndY=65 EndZ=0
    g4: LineSegment StartX=-9.21183 StartY=65 StartZ=0 EndX=-7.64206 EndY=69.26 EndZ=0
    g5: LineSegment StartX=-7.64206 StartY=69.26 StartZ=0 EndX=-3.31416 EndY=69.26 EndZ=0
    g6: LineSegment StartX=-3.31416 StartY=69.26 StartZ=0 EndX=0.811065 EndY=65 EndZ=0
  constraints (20):
    c: Horizontal(g0)
    c: Coincident(g1,g-3)
    c: Coincident(g1,g0)
    c: PointOnObject(g2,g-4)
    c: Coincident(g2,g0)
    c: Tangent(g0,g-5)
    c: Parallel(g1,g-3)
    c: Angle(g2,g-4) = 2.35619
    c: Tangent(g2,g-6)
    c: Coincident(g3,g2)
    c: Horizontal(g3)
    c: Coincident(g4,g3)
    c: Coincident(g5,g4)
    c: Horizontal(g5)
    c: Coincident(g6,g5)
    c: Coincident(g6,g1)
    c: Distance(g3,g3) = 4.23
    c: Distance(g6,g6) = 5.93
    c: Distance(g4,g4) = 4.54
    c: Distance(g4,g0) = 1.18
FEATURE [PartDesign::Pad] Pad008
  BaseFeature = -> Pocket006
  Direction = (0,1,-2e-16)
  Length = 10
  Length2 = 10
  Profile = -> Sketch008
  ReferenceAxis = -> Sketch008 [N_Axis]
  Refine = true
  Suppressed = false
  Type = 3
  UpToFace = -> Pocket006 [Face8]
FEATURE [Sketcher::SketchObject] Sketch009
  ArcFitTolerance = 1e-06
  AttachmentSupport = -> [Pad008]
  ExternalGeometry = -> [Pad008]
  FullyConstrained = true
  MakeInternals = false
  MapMode = 5
  Placement = pos=(0,24.2,0) rot=(0,0.707107,0.707107;3.14159rad)
  sketch-geometry (3):
    g0: LineSegment StartX=-2.10592 StartY=70.44 StartZ=0 EndX=3.72819 EndY=59.5597 EndZ=0
    g1: LineSegment StartX=3.72819 StartY=59.5597 StartZ=0 EndX=3.72819 EndY=70.44 EndZ=0
    g2: LineSegment StartX=3.72819 StartY=70.44 StartZ=0 EndX=-2.10592 EndY=70.44 EndZ=0
  constraints (7):
    c: Coincident(g0,g-4)
    c: Coincident(g0,g-3)
    c: Coincident(g1,g0)
    c: Vertical(g1)
    c: Coincident(g2,g1)
    c: Coincident(g2,g0)
    c: Horizontal(g2)
FEATURE [PartDesign::Pocket] Pocket007
  BaseFeature = -> Pad008
  Direction = (0,-1,2e-16)
  Length = 5
  Length2 = 5
  Profile = -> Sketch009
  ReferenceAxis = -> Sketch009 [N_Axis]
  Refine = true
  Suppressed = false
  Type = 0
FEATURE [Sketcher::SketchObject] Sketch010
  ArcFitTolerance = 1e-06
  AttachmentSupport = -> [Pocket007]
  ExternalGeometry = -> [Pocket007]
  FullyConstrained = true
  MakeInternals = false
  MapMode = 5
  Placement = pos=(0,0,1.4e-15) rot=(1,0,0;3.14159rad)
  sketch-geometry (2):
    g0: Circle CenterX=-7.58 CenterY=8.4625 CenterZ=0 NormalX=0 NormalY=0 NormalZ=1 AngleXU=0 Radius=1.6
    g1: Circle CenterX=-7.58 CenterY=-8.4625 CenterZ=0 NormalX=0 NormalY=0 NormalZ=1 AngleXU=0 Radius=1.6
  constraints (5):
    c: Symmetric(g0,g1,g-1)
    c: Equal(g0,g1)
    c: Distance(g0,g-3) = 15.7375
    c: Distance(g0,g-4) = 9.8
    c: Diameter(g0) = 3.2
FEATURE [PartDesign::Pocket] Pocket008
  BaseFeature = -> Pocket007
  Direction = (0,0,1)
  Length = 7
  Length2 = 5
  Profile = -> Sketch010
  ReferenceAxis = -> Sketch010 [N_Axis]
  Refine = true
  Suppressed = false
  Type = 0
FEATURE [Sketcher::SketchObject] Sketch011
  ArcFitTolerance = 1e-06
  AttachmentSupport = -> [Pocket008]
  ExternalGeometry = -> [Pocket008]
  FullyConstrained = true
  MakeInternals = false
  MapMode = 5
  Placement = pos=(0,0,1.4e-15) rot=(1,0,0;3.14159rad)
  sketch-geometry (6):
    g0: LineSegment StartX=-17.38 StartY=5 StartZ=0 EndX=-17.38 EndY=-5 EndZ=0
    g1: LineSegment StartX=-17.38 StartY=-5 StartZ=0 EndX=-6.38 EndY=-5 EndZ=0
    g2: LineSegment StartX=-17.38 StartY=5 StartZ=0 EndX=-6.38 EndY=5 EndZ=0
    g3: LineSegment StartX=-6.38 StartY=5 StartZ=0 EndX=2.91 EndY=14.1 EndZ=0
    g4: LineSegment StartX=-6.38 StartY=-5 StartZ=0 EndX=2.91 EndY=-14.1 EndZ=0
    g5: LineSegment StartX=2.91 StartY=-14.1 StartZ=0 EndX=2.91 EndY=14.1 EndZ=0
  constraints (15):
    c: PointOnObject(g0,g-3)
    c: Coincident(g1,g0)
    c: Horizontal(g1)
    c: Coincident(g2,g0)
    c: Horizontal(g2)
    c: Coincident(g3,g2)
    c: Coincident(g3,g-4)
    c: Coincident(g4,g1)
    c: Coincident(g4,g-4)
    c: Coincident(g5,g4)
    c: Coincident(g5,g3)
    c: Equal(g2,g1)
    c: Symmetric(g0,g0,g-1)
    c: Distance(g0,g0) = 10
    c: Distance(g2,g2) = 11
FEATURE [PartDesign::Pocket] Pocket009
  BaseFeature = -> Pocket008
  Direction = (0,0,1)
  Length = 1
  Length2 = 5
  Profile = -> Sketch011
  ReferenceAxis = -> Sketch011 [N_Axis]
  Refine = true
  Suppressed = false
  Type = 0
FEATURE [PartDesign::Body] Body  label="k1_toolhead"
  AllowCompound = false
  BaseFeature = -> Part__Feature
  Group = -> [BaseFeature,Sketch,Pad,Fillet,Pad001,Pad002,DatumLine,DatumLine001,Pad003,Pad004,Pad005,Pad006,Pad007,Sketch001,Pocket,Sketch002,Pocket001,Sketch003,Pocket002,Sketch004,Pocket003,Sketch005,Pocket004,Fillet001,Sketch006,Pocket005,Sketch007,Pocket006,Sketch008,Pad008,Sketch009,Pocket007,Sketch010,Pocket008,Sketch011,Pocket009]
  Origin = -> Origin
  Tip = -> Pocket009
FEATURE [App::Part] Part  label="k1_toolhead_part"
  Group = -> [Part__Feature,Body,Link,Link001,Link002,Link003,Link004,Link005,Link006,Link007,Link008]
  Origin = -> Origin001
COMPONENT P10 — recipe-attached ("rail_mgn013", a linked part whose construction recipe lives in a companion FreeCAD document of the same project; that document's serialized recipe follows).
Construction recipe (the companion document, serialized — sketch geometry with constraints, then the solid features built on it; lengths are millimeters unless a unit is written):

FCSTD DOCUMENT  (FreeCAD 1.0R38641 +468 (Git))
Label: cad_rail_mgn12
License: All rights reserved
LicenseURL: https://en.wikipedia.org/wiki/All_rights_reserved
objects: PartDesign::Line×4, Sketcher::SketchObject×2, PartDesign::Pad×1, PartDesign::Pocket×1, PartDesign::LinearPattern×1, PartDesign::Plane×1, PartDesign::Body×1
note: 18 computed .brp shape members not serialized (recipe doc carries the construction recipe); baked Part::Feature solids carry a one-line shape summary decoded from their .brp

FEATURE [Sketcher::SketchObject] Sketch
  ArcFitTolerance = 0
  AttachmentSupport = -> [XY_Plane]
  FullyConstrained = true
  MakeInternals = false
  MapMode = 5
  sketch-geometry (4):
    g0: LineSegment StartX=-6 StartY=4 StartZ=0 EndX=6 EndY=4 EndZ=0
    g1: LineSegment StartX=6 StartY=4 StartZ=0 EndX=6 EndY=-4 EndZ=0
    g2: LineSegment StartX=6 StartY=-4 StartZ=0 EndX=-6 EndY=-4 EndZ=0
    g3: LineSegment StartX=-6 StartY=-4 StartZ=0 EndX=-6 EndY=4 EndZ=0
  constraints (10):
    c: Coincident(g0,g1)
    c: Coincident(g1,g2)
    c: Coincident(g2,g3)
    c: Coincident(g3,g0)
    c: Horizontal(g2)
    c: Vertical(g1)
    c: Symmetric(g0,g0,g-2)
    c: Symmetric(g0,g2,g-1)
    c: Distance(g0) = 12
    c: Distance(g3) = 8
FEATURE [PartDesign::Pad] Pad
  Direction = (0,0,1)
  Length = 310
  Length2 = 10
  Profile = -> Sketch
  ReferenceAxis = -> Sketch [N_Axis]
  Suppressed = false
  Type = 0
FEATURE [Sketcher::SketchObject] Sketch001
  ArcFitTolerance = 0
  AttachmentSupport = -> [Pad]
  ExternalGeometry = -> [Pad]
  FullyConstrained = true
  MakeInternals = false
  MapMode = 5
  Placement = pos=(0,-4,0) rot=(1,0,0;1.5708rad)
  sketch-geometry (1):
    g0: Circle CenterX=0 CenterY=305 CenterZ=0 NormalX=0 NormalY=0 NormalZ=1 AngleXU=0 Radius=1.5
  constraints (3):
    c: PointOnObject(g0,g-2)
    c: Radius(g0) = 1.5
    c: Distance(g0,g-3) = 5
FEATURE [PartDesign::Pocket] Pocket
  BaseFeature = -> Pad
  Direction = (0,1,-2e-16)
  Length = 5
  Length2 = 5
  Profile = -> Sketch001
  ReferenceAxis = -> Sketch001 [N_Axis]
  Suppressed = false
  Type = 1
FEATURE [PartDesign::LinearPattern] LinearPattern
  BaseFeature = -> Pocket
  Direction = -> Z_Axis
  Length = 300
  Mode = 0
  Occurrences = 13
  Offset = 25
  Originals = -> [Pocket]
  Reversed = true
  Suppressed = false
  TransformMode = 0
FEATURE [PartDesign::Line] HoleAxis_1  label="HoleAxis_left"
  AttacherType = Attacher::AttachEngineLine
  AttachmentSupport = -> [LinearPattern]
  Length = 4.2272
  MapMode = 19
  Placement = pos=(0,-4,305) rot=(1,0,0;1.5708rad)
  ResizeMode = 1
FEATURE [PartDesign::Line] HoleAxis_2  label="HoleAxis_right"
  AttacherType = Attacher::AttachEngineLine
  AttachmentSupport = -> [LinearPattern]
  Length = 4.2272
  MapMode = 19
  Placement = pos=(-3.31e-14,-4,5) rot=(1,0,0;1.5708rad)
  ResizeMode = 1
FEATURE [PartDesign::Plane] DatumPlane  label="Plane_caret"
  AttachmentSupport = -> [LinearPattern]
  Length = 75.8844
  MapMode = 5
  Placement = pos=(0,-4,0) rot=(1,0,0;1.5708rad)
  ResizeMode = 0
  Width = 360.884
FEATURE [PartDesign::Line] HoleAxis_3  label="HoleAxis_right_frame"
  AttacherType = Attacher::AttachEngineLine
  AttachmentSupport = -> [LinearPattern]
  Length = 4.2272
  MapMode = 19
  Placement = pos=(-3.33e-14,4,5) rot=(1,0,0;1.5708rad)
  ResizeMode = 1
FEATURE [PartDesign::Line] HoleAxis_4  label="HoleAxis_left_frame"
  AttacherType = Attacher::AttachEngineLine
  AttachmentSupport = -> [LinearPattern]
  Length = 4.2272
  MapMode = 19
  Placement = pos=(0,4,305) rot=(1,0,0;1.5708rad)
  ResizeMode = 1
FEATURE [PartDesign::Body] Body  label="rail_mgn12"
  AllowCompound = false
  Group = -> [Sketch,Pad,Sketch001,Pocket,LinearPattern,HoleAxis_1,HoleAxis_2,DatumPlane,HoleAxis_3,HoleAxis_4]
  Origin = -> Origin
  Placement = pos=(0,6,4) rot=(0.57735,0.57735,0.57735;2.0944rad)
  Tip = -> LinearPattern
COMPONENT P11 — same part as P10; its construction recipe is shown at P10.
PROVENANCE & LICENSES
A FreeCAD (.FCStd) document from a public repository crawl; recipes are the document's own serialized feature recipes (and, for linked parts, companion documents' recipes).
License: as declared in the source repository (recorded in the dataset sidecar).
